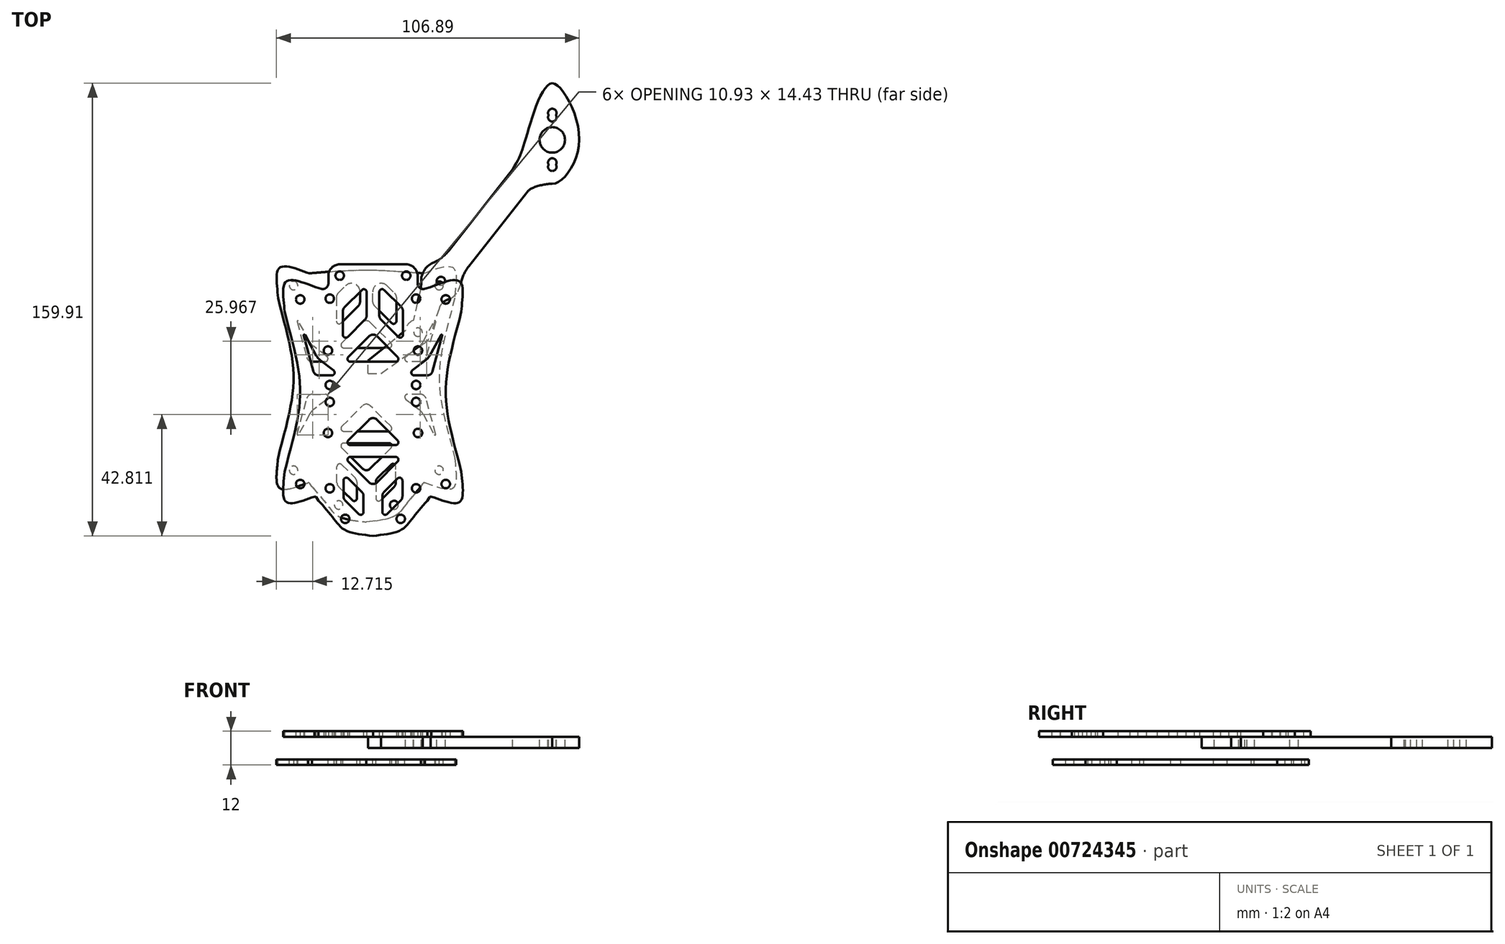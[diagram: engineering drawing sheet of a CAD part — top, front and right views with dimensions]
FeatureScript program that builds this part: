
annotation { "Feature Type Name" : "Feature", "Feature Type Description" : "" }
export const myFeature = defineFeature(function(context is Context, id is Id, definition is map)
    precondition{}
    {
        {
            var Q0;
            Q0=qCreatedBy(makeId("Top.planeOp"),FACE);
            var sketch = newSketch(context, id + "F0", { "sketchPlane" : qUnion([Q0])});
            skPoint(sketch, "E0.middle", {"position": v(0, -4.73) * mm});
            skLineSegment(sketch, "E1.bottom", {"start": v(25.7, 27.89) * mm, "end": v(-25.7, 27.89) * mm, "construction": true});
            skLineSegment(sketch, "E1.top", {"start": v(25.7, -37.35) * mm, "end": v(-25.7, -37.35) * mm, "construction": true});
            skLineSegment(sketch, "E1.left", {"start": v(25.7, 27.89) * mm, "end": v(25.7, -37.35) * mm, "construction": true});
            skLineSegment(sketch, "E1.right", {"start": v(-25.7, 27.89) * mm, "end": v(-25.7, -37.35) * mm, "construction": true});
            skLineSegment(sketch, "E2.bottom", {"start": v(-65, 77.77) * mm, "end": v(65, 77.77) * mm, "construction": true});
            skLineSegment(sketch, "E2.top", {"start": v(-65, -87.23) * mm, "end": v(65, -87.23) * mm, "construction": true});
            skLineSegment(sketch, "E2.left", {"start": v(-65, 77.77) * mm, "end": v(-65, -87.23) * mm, "construction": true});
            skLineSegment(sketch, "E2.right", {"start": v(65, 77.77) * mm, "end": v(65, -87.23) * mm, "construction": true});
            skCircle(sketch, "E3", {"center": v(65, 77.77) * mm, "radius": 4.5 * mm, "construction": true});
            skCircle(sketch, "E4", {"center": v(-65, 77.77) * mm, "radius": 4.5 * mm, "construction": true});
            skCircle(sketch, "E5", {"center": v(65, -87.23) * mm, "radius": 4.5 * mm, "construction": true});
            skCircle(sketch, "E6", {"center": v(-65, -87.23) * mm, "radius": 4.5 * mm, "construction": true});
            skCircle(sketch, "E7", {"center": v(65, 77.77) * mm, "radius": 8 * mm, "construction": true});
            skCircle(sketch, "E8", {"center": v(65, -87.23) * mm, "radius": 8 * mm, "construction": true});
            skCircle(sketch, "E9", {"center": v(-65, -87.23) * mm, "radius": 8 * mm, "construction": true});
            skCircle(sketch, "E10", {"center": v(-65, 77.77) * mm, "radius": 8 * mm, "construction": true});
            skCircle(sketch, "E11", {"center": v(65, 77.77) * mm, "radius": 9.5 * mm, "construction": true});
            skCircle(sketch, "E12", {"center": v(65, -87.23) * mm, "radius": 9.5 * mm, "construction": true});
            skCircle(sketch, "E13", {"center": v(-65, -87.23) * mm, "radius": 9.5 * mm, "construction": true});
            skCircle(sketch, "E14", {"center": v(-65, 77.77) * mm, "radius": 9.5 * mm, "construction": true});
            skCircle(sketch, "E15", {"center": v(65, 77.77) * mm, "radius": 14 * mm, "construction": true});
            skCircle(sketch, "E16", {"center": v(-65, 77.77) * mm, "radius": 14 * mm, "construction": true});
            skCircle(sketch, "E17", {"center": v(65, -87.23) * mm, "radius": 14 * mm, "construction": true});
            skCircle(sketch, "E18", {"center": v(-65, -87.23) * mm, "radius": 14 * mm, "construction": true});
            skCircle(sketch, "E19", {"center": v(65, 77.77) * mm, "radius": 63.5 * mm, "construction": true});
            skCircle(sketch, "E20", {"center": v(65, -87.23) * mm, "radius": 63.5 * mm, "construction": true});
            skCircle(sketch, "E21", {"center": v(-65, -87.23) * mm, "radius": 63.5 * mm, "construction": true});
            skCircle(sketch, "E22", {"center": v(-65, 77.77) * mm, "radius": 63.5 * mm, "construction": true});
            skLineSegment(sketch, "E23.bottom", {"start": v(-26.2, 21.46) * mm, "end": v(26.2, 21.46) * mm, "construction": true});
            skLineSegment(sketch, "E23.top", {"start": v(-26.19, -30.92) * mm, "end": v(26.2, -30.92) * mm, "construction": true});
            skLineSegment(sketch, "E23.left", {"start": v(-26.2, 21.46) * mm, "end": v(-26.2, -30.92) * mm, "construction": true});
            skLineSegment(sketch, "E23.right", {"start": v(26.2, 21.46) * mm, "end": v(26.2, -30.92) * mm, "construction": true});
            skCircle(sketch, "E24", {"center": v(25.7, 27.89) * mm, "radius": 1.5 * mm, "construction": true});
            skCircle(sketch, "E25", {"center": v(-25.7, 27.89) * mm, "radius": 1.5 * mm, "construction": true});
            skCircle(sketch, "E26", {"center": v(25.7, -37.35) * mm, "radius": 1.5 * mm, "construction": true});
            skCircle(sketch, "E27", {"center": v(-25.7, -37.35) * mm, "radius": 1.5 * mm, "construction": true});
            skLineSegment(sketch, "E28", {"start": v(-65, 77.77) * mm, "end": v(65, -87.23) * mm, "construction": true});
            skLineSegment(sketch, "E29", {"start": v(65, 77.77) * mm, "end": v(-65, -87.23) * mm, "construction": true});
            skLineSegment(sketch, "E30.bottom", {"start": v(-15.25, -8.35) * mm, "end": v(15.25, -8.35) * mm, "construction": true});
            skLineSegment(sketch, "E30.top", {"start": v(-15.25, -38.85) * mm, "end": v(15.25, -38.85) * mm, "construction": true});
            skLineSegment(sketch, "E30.left", {"start": v(-15.25, -8.35) * mm, "end": v(-15.25, -38.85) * mm, "construction": true});
            skLineSegment(sketch, "E30.right", {"start": v(15.25, -8.35) * mm, "end": v(15.25, -38.85) * mm, "construction": true});
            skPoint(sketch, "E30.middle", {"position": v(0, -23.6) * mm});
            skLineSegment(sketch, "E31.bottom", {"start": v(-15.25, 28.15) * mm, "end": v(15.25, 28.15) * mm, "construction": true});
            skLineSegment(sketch, "E31.top", {"start": v(-15.25, -2.35) * mm, "end": v(15.25, -2.35) * mm, "construction": true});
            skLineSegment(sketch, "E31.left", {"start": v(-15.25, 28.15) * mm, "end": v(-15.25, -2.35) * mm, "construction": true});
            skLineSegment(sketch, "E31.right", {"start": v(15.25, 28.15) * mm, "end": v(15.25, -2.35) * mm, "construction": true});
            skPoint(sketch, "E31.middle", {"position": v(0, 12.9) * mm});
            skLineSegment(sketch, "E32", {"start": v(0, -2.35) * mm, "end": v(0, -8.35) * mm, "construction": true});
            skLineSegment(sketch, "E33", {"start": v(0, 36.28) * mm, "end": v(-11.75, 36.28) * mm, "construction": true});
            skLineSegment(sketch, "E34", {"start": v(0, 36.28) * mm, "end": v(11.75, 36.28) * mm, "construction": true});
            skLineSegment(sketch, "E35", {"start": v(-25.7, 27.89) * mm, "end": v(-20.2, 32.22) * mm, "construction": true});
            skLineSegment(sketch, "E36", {"start": v(-25.7, 27.89) * mm, "end": v(-31.2, 23.56) * mm, "construction": true});
            skLineSegment(sketch, "E37", {"start": v(-25.7, 27.89) * mm, "end": v(-30.65, 34.17) * mm, "construction": true});
            skLineSegment(sketch, "E38", {"start": v(25.7, 27.89) * mm, "end": v(30.65, 34.17) * mm, "construction": true});
            skLineSegment(sketch, "E39", {"start": v(25.7, 27.89) * mm, "end": v(20.2, 32.22) * mm, "construction": true});
            skLineSegment(sketch, "E40", {"start": v(25.7, 27.89) * mm, "end": v(31.2, 23.56) * mm, "construction": true});
            skLineSegment(sketch, "E41", {"start": v(25.7, -37.35) * mm, "end": v(30.65, -43.64) * mm, "construction": true});
            skLineSegment(sketch, "E42", {"start": v(25.7, -37.35) * mm, "end": v(20.2, -41.68) * mm, "construction": true});
            skLineSegment(sketch, "E43", {"start": v(25.7, -37.35) * mm, "end": v(31.2, -33.02) * mm, "construction": true});
            skLineSegment(sketch, "E44", {"start": v(-25.7, -37.35) * mm, "end": v(-30.65, -43.64) * mm, "construction": true});
            skLineSegment(sketch, "E45", {"start": v(-25.7, -37.35) * mm, "end": v(-20.2, -41.68) * mm, "construction": true});
            skLineSegment(sketch, "E46", {"start": v(-25.7, -37.35) * mm, "end": v(-31.2, -33.02) * mm, "construction": true});
            skFitSpline(sketch, "E47", {"points": [v(-20.2, 32.22) * mm, v(-30.65, 34.17) * mm, v(-31.2, 23.56) * mm], "startDerivative": vector(-20.3, 7.46) * mm, "endDerivative": vector(0.93, -21.61) * mm});
            skFitSpline(sketch, "E48", {"points": [v(20.2, 32.22) * mm, v(30.65, 34.17) * mm, v(31.2, 23.56) * mm], "startDerivative": vector(20.3, 7.46) * mm, "endDerivative": vector(-0.93, -21.61) * mm});
            skLineSegment(sketch, "E49", {"start": v(-11.75, 36.28) * mm, "end": v(-15.75, 36.28) * mm, "construction": true});
            skLineSegment(sketch, "E50", {"start": v(11.75, 36.28) * mm, "end": v(15.75, 36.28) * mm, "construction": true});
            skCircle(sketch, "E51", {"center": v(-11.75, 36.28) * mm, "radius": 1.5 * mm});
            skCircle(sketch, "E52", {"center": v(11.75, 36.28) * mm, "radius": 1.5 * mm});
            skLineSegment(sketch, "E53", {"start": v(0, 36.28) * mm, "end": v(0, 40.28) * mm, "construction": true});
            skLineSegment(sketch, "E54", {"start": v(-15.75, 36.28) * mm, "end": v(-15.75, 36.28) * mm});
            skLineSegment(sketch, "E55", {"start": v(-11.75, 40.28) * mm, "end": v(0, 40.28) * mm});
            skLineSegment(sketch, "E56", {"start": v(0, 40.28) * mm, "end": v(11.75, 40.28) * mm});
            skLineSegment(sketch, "E57", {"start": v(15.75, 36.28) * mm, "end": v(15.75, 36.28) * mm});
            skPoint(sketch, "E58.visualSharp", {"position": v(-15.75, 40.28) * mm});
            skArc(sketch, "E58.filletArc", {"start": v(-11.75, 40.28) * mm, "mid": v(-14.58, 39.1) * mm, "end": v(-15.75, 36.28) * mm});
            skPoint(sketch, "E59.visualSharp", {"position": v(15.75, 40.28) * mm});
            skArc(sketch, "E59.filletArc", {"start": v(15.75, 36.28) * mm, "mid": v(14.58, 39.1) * mm, "end": v(11.75, 40.28) * mm});
            skLineSegment(sketch, "E60", {"start": v(-20.2, 32.22) * mm, "end": v(-18.34, 31.65) * mm});
            skLineSegment(sketch, "E61", {"start": v(-15.75, 33.56) * mm, "end": v(-15.75, 36.28) * mm});
            skPoint(sketch, "E62.visualSharp", {"position": v(-15.75, 30.85) * mm});
            skArc(sketch, "E62.filletArc", {"start": v(-18.34, 31.65) * mm, "mid": v(-16.56, 31.95) * mm, "end": v(-15.75, 33.56) * mm});
            skLineSegment(sketch, "E63", {"start": v(-15.75, 30.85) * mm, "end": v(0, 30.85) * mm, "construction": true});
            skLineSegment(sketch, "E64", {"start": v(0, 30.85) * mm, "end": v(15.75, 30.85) * mm, "construction": true});
            skLineSegment(sketch, "E65", {"start": v(20.2, 32.22) * mm, "end": v(18.34, 31.65) * mm});
            skLineSegment(sketch, "E66", {"start": v(15.75, 36.28) * mm, "end": v(15.75, 33.56) * mm});
            skPoint(sketch, "E67.visualSharp", {"position": v(15.75, 30.85) * mm});
            skArc(sketch, "E67.filletArc", {"start": v(15.75, 33.56) * mm, "mid": v(16.56, 31.95) * mm, "end": v(18.34, 31.65) * mm});
            skCircle(sketch, "E68", {"center": v(-15.25, -38.85) * mm, "radius": 1.5 * mm});
            skCircle(sketch, "E69", {"center": v(15.25, -38.85) * mm, "radius": 1.5 * mm});
            skLineSegment(sketch, "E70", {"start": v(0, -38.85) * mm, "end": v(0, -42.85) * mm, "construction": true});
            skLineSegment(sketch, "E71", {"start": v(-15.25, -38.85) * mm, "end": v(-19.25, -38.85) * mm, "construction": true});
            skLineSegment(sketch, "E72", {"start": v(15.25, -38.85) * mm, "end": v(19.25, -38.85) * mm, "construction": true});
            skLineSegment(sketch, "E73", {"start": v(-19.25, -43.2) * mm, "end": v(0, -43.2) * mm, "construction": true});
            skLineSegment(sketch, "E74", {"start": v(0, -43.2) * mm, "end": v(19.25, -43.2) * mm, "construction": true});
            skPoint(sketch, "E75.visualSharp", {"position": v(-19.25, -43.2) * mm});
            skPoint(sketch, "E76.visualSharp", {"position": v(19.25, -43.2) * mm});
            skCircle(sketch, "E77", {"center": v(-9.8, -49.64) * mm, "radius": 1.5 * mm});
            skCircle(sketch, "E78", {"center": v(9.8, -49.64) * mm, "radius": 1.5 * mm});
            skLineSegment(sketch, "E79", {"start": v(-9.8, -49.64) * mm, "end": v(0, -49.64) * mm, "construction": true});
            skLineSegment(sketch, "E80", {"start": v(0, -49.64) * mm, "end": v(9.8, -49.64) * mm, "construction": true});
            skFitSpline(sketch, "E81", {"points": [v(-31.2, 23.56) * mm, v(-25.7, -4.73) * mm, v(-31.2, -33.02) * mm], "startDerivative": vector(16.96, -67.18) * mm, "endDerivative": vector(-16.96, -67.18) * mm});
            skFitSpline(sketch, "E82", {"points": [v(31.2, 23.56) * mm, v(25.7, -4.73) * mm, v(31.2, -33.02) * mm], "startDerivative": vector(-16.96, -67.18) * mm, "endDerivative": vector(16.96, -67.18) * mm});
            skLineSegment(sketch, "E83", {"start": v(0, -49.64) * mm, "end": v(0, -55.64) * mm, "construction": true});
            skLineSegment(sketch, "E84", {"start": v(-9.8, -49.64) * mm, "end": v(-13.8, -49.64) * mm, "construction": true});
            skLineSegment(sketch, "E85", {"start": v(-9.8, -49.64) * mm, "end": v(-9.8, -53.64) * mm, "construction": true});
            skLineSegment(sketch, "E86", {"start": v(9.8, -49.64) * mm, "end": v(13.8, -49.64) * mm, "construction": true});
            skLineSegment(sketch, "E87", {"start": v(9.8, -49.64) * mm, "end": v(9.8, -53.64) * mm, "construction": true});
            skCircle(sketch, "E88", {"center": v(-25.7, 27.89) * mm, "radius": 1.5 * mm});
            skCircle(sketch, "E89", {"center": v(25.7, 27.89) * mm, "radius": 1.5 * mm});
            skCircle(sketch, "E90", {"center": v(-25.7, -37.35) * mm, "radius": 1.5 * mm});
            skCircle(sketch, "E91", {"center": v(25.7, -37.35) * mm, "radius": 1.5 * mm});
            skLineSegment(sketch, "E92", {"start": v(0, 27.89) * mm, "end": v(0, 36.28) * mm, "construction": true});
            skLineSegment(sketch, "E93", {"start": v(117.55, -29.37) * mm, "end": v(117.55, 4.6) * mm, "construction": true});
            skLineSegment(sketch, "E94", {"start": v(-19.04, -41.25) * mm, "end": v(0, -41.25) * mm, "construction": true});
            skLineSegment(sketch, "E95", {"start": v(0, -41.25) * mm, "end": v(19.04, -41.25) * mm, "construction": true});
            skFitSpline(sketch, "E96", {"points": [v(-19.25, -43.2) * mm, v(-13.8, -49.64) * mm, v(-9.8, -53.64) * mm, v(0, -55.64) * mm], "startDerivative": vector(17.01, -18.5) * mm, "endDerivative": vector(29.8, -3.11) * mm});
            skFitSpline(sketch, "E97", {"points": [v(19.25, -43.2) * mm, v(13.8, -49.64) * mm, v(9.8, -53.64) * mm, v(0, -55.64) * mm], "startDerivative": vector(-17.98, -19.6) * mm, "endDerivative": vector(-29.8, -3.11) * mm});
            skLineSegment(sketch, "E98", {"start": v(118.58, 5.6) * mm, "end": v(171.8, 3.95) * mm, "construction": true});
            skPoint(sketch, "E99.visualSharp", {"position": v(117.55, 5.63) * mm});
            skArc(sketch, "E99.filletArc", {"start": v(118.58, 5.6) * mm, "mid": v(117.85, 5.32) * mm, "end": v(117.55, 4.6) * mm, "construction": true});
            skPoint(sketch, "E100.visualSharp", {"position": v(19.04, -41.25) * mm});
            skPoint(sketch, "E101.visualSharp", {"position": v(-19.04, -41.25) * mm});
            skLineSegment(sketch, "E102.bottom", {"start": v(-13.78, 12.77) * mm, "end": v(13.78, 12.77) * mm, "construction": true});
            skLineSegment(sketch, "E102.top", {"start": v(-13.78, -22.23) * mm, "end": v(13.78, -22.23) * mm, "construction": true});
            skLineSegment(sketch, "E102.left", {"start": v(-13.78, 12.77) * mm, "end": v(-13.78, -22.23) * mm, "construction": true});
            skLineSegment(sketch, "E102.right", {"start": v(13.78, 12.77) * mm, "end": v(13.78, -22.23) * mm, "construction": true});
            skCircle(sketch, "E103", {"center": v(-15.25, -8.35) * mm, "radius": 1.5 * mm});
            skCircle(sketch, "E104", {"center": v(15.25, -8.35) * mm, "radius": 1.5 * mm});
            skCircle(sketch, "E105", {"center": v(15.25, -2.35) * mm, "radius": 1.5 * mm});
            skCircle(sketch, "E106", {"center": v(-15.25, -2.35) * mm, "radius": 1.5 * mm});
            skCircle(sketch, "E107", {"center": v(-15.25, 28.15) * mm, "radius": 1.5 * mm});
            skCircle(sketch, "E108", {"center": v(15.25, 28.15) * mm, "radius": 1.5 * mm});
            skLineSegment(sketch, "E109", {"start": v(0, 8.34) * mm, "end": v(-18.2, 8.34) * mm, "construction": true});
            skLineSegment(sketch, "E110", {"start": v(0, 8.34) * mm, "end": v(18.2, 8.34) * mm, "construction": true});
            skLineSegment(sketch, "E111", {"start": v(0, -4.73) * mm, "end": v(0, 9.53) * mm, "construction": true});
            skLineSegment(sketch, "E112", {"start": v(0, -4.73) * mm, "end": v(17, -4.73) * mm, "construction": true});
            skLineSegment(sketch, "E113.bottom", {"start": v(-15.9, 9.82) * mm, "end": v(15.9, 9.82) * mm, "construction": true});
            skLineSegment(sketch, "E113.top", {"start": v(-15.9, -19.29) * mm, "end": v(15.9, -19.29) * mm, "construction": true});
            skLineSegment(sketch, "E113.left", {"start": v(-15.9, 9.82) * mm, "end": v(-15.9, -19.29) * mm, "construction": true});
            skLineSegment(sketch, "E113.right", {"start": v(15.9, 9.82) * mm, "end": v(15.9, -19.29) * mm, "construction": true});
            skCircle(sketch, "E114", {"center": v(15.9, 9.82) * mm, "radius": 1.5 * mm});
            skCircle(sketch, "E115", {"center": v(15.9, -19.29) * mm, "radius": 1.5 * mm});
            skCircle(sketch, "E116", {"center": v(-15.9, -19.29) * mm, "radius": 1.5 * mm});
            skCircle(sketch, "E117", {"center": v(-15.9, 9.82) * mm, "radius": 1.5 * mm});
            skLineSegment(sketch, "E118", {"start": v(0, 21.19) * mm, "end": v(14.33, 21.19) * mm, "construction": true});
            skLineSegment(sketch, "E119", {"start": v(0, 21.19) * mm, "end": v(-14.33, 21.19) * mm, "construction": true});
            skPoint(sketch, "E120.middle", {"position": v(-14.33, 21.19) * mm});
            skPoint(sketch, "E121.middle", {"position": v(14.33, 21.19) * mm});
            skFitSpline(sketch, "E122", {"points": [v(-31.2, -33.02) * mm, v(-30.65, -43.64) * mm, v(-20.6, -41.83) * mm], "startDerivative": vector(-1.92, -24.87) * mm, "endDerivative": vector(23.17, 7.34) * mm});
            skLineSegment(sketch, "E123", {"start": v(-20.6, -41.83) * mm, "end": v(0, -41.83) * mm, "construction": true});
            skLineSegment(sketch, "E124", {"start": v(0, -41.83) * mm, "end": v(20.6, -41.83) * mm, "construction": true});
            skLineSegment(sketch, "E125", {"start": v(19.25, -43.2) * mm, "end": v(19.99, -42.02) * mm});
            skLineSegment(sketch, "E126", {"start": v(20.58, -41.82) * mm, "end": v(20.6, -41.83) * mm});
            skLineSegment(sketch, "E127", {"start": v(-19.25, -43.2) * mm, "end": v(-19.99, -42.02) * mm});
            skLineSegment(sketch, "E128", {"start": v(-20.58, -41.82) * mm, "end": v(-20.6, -41.83) * mm});
            skLineSegment(sketch, "E129", {"start": v(171.8, 3.95) * mm, "end": v(171.8, -18.5) * mm, "construction": true});
            skPoint(sketch, "E130.visualSharp", {"position": v(20.2, -41.68) * mm});
            skArc(sketch, "E130.filletArc", {"start": v(20.58, -41.82) * mm, "mid": v(20.25, -41.82) * mm, "end": v(19.99, -42.02) * mm});
            skPoint(sketch, "E131.visualSharp", {"position": v(-20.2, -41.68) * mm});
            skArc(sketch, "E131.filletArc", {"start": v(-19.99, -42.02) * mm, "mid": v(-20.25, -41.82) * mm, "end": v(-20.58, -41.82) * mm});
            skLineSegment(sketch, "E132", {"start": v(0, -4.73) * mm, "end": v(0, -1.43) * mm, "construction": true});
            skLineSegment(sketch, "E133.bottom", {"start": v(-5.5, 0.77) * mm, "end": v(5.5, 0.77) * mm, "construction": true});
            skLineSegment(sketch, "E133.top", {"start": v(-5.5, -10.23) * mm, "end": v(5.5, -10.23) * mm, "construction": true});
            skLineSegment(sketch, "E133.left", {"start": v(-5.5, 0.77) * mm, "end": v(-5.5, -10.23) * mm, "construction": true});
            skLineSegment(sketch, "E133.right", {"start": v(5.5, 0.77) * mm, "end": v(5.5, -10.23) * mm, "construction": true});
            skLineSegment(sketch, "E134.bottom", {"start": v(-7.98, 5.89) * mm, "end": v(7.98, 5.89) * mm});
            skPoint(sketch, "E134.middle", {"position": v(0, 7.86) * mm});
            skPoint(sketch, "E135.middle", {"position": v(0, -31.33) * mm});
            skPoint(sketch, "E136", {"position": v(0, -22.23) * mm});
            skPoint(sketch, "E137", {"position": v(0, -30.92) * mm});
            skLineSegment(sketch, "E138", {"start": v(-8.69, 7.6) * mm, "end": v(-1.41, 14.87) * mm});
            skLineSegment(sketch, "E139", {"start": v(1.41, 14.87) * mm, "end": v(8.69, 7.6) * mm});
            skPoint(sketch, "E140.visualSharp", {"position": v(0, 16.28) * mm});
            skArc(sketch, "E140.filletArc", {"start": v(1.41, 14.87) * mm, "mid": v(0, 15.46) * mm, "end": v(-1.41, 14.87) * mm});
            skPoint(sketch, "E141.visualSharp", {"position": v(-10.4, 5.89) * mm});
            skArc(sketch, "E141.filletArc", {"start": v(-8.69, 7.6) * mm, "mid": v(-8.9, 6.5) * mm, "end": v(-7.98, 5.89) * mm});
            skPoint(sketch, "E142.visualSharp", {"position": v(10.4, 5.89) * mm});
            skArc(sketch, "E142.filletArc", {"start": v(7.98, 5.89) * mm, "mid": v(8.9, 6.5) * mm, "end": v(8.69, 7.6) * mm});
            skPoint(sketch, "E143.visualSharp", {"position": v(0, -4.14) * mm});
            skLineSegment(sketch, "E144", {"start": v(1, 5.89) * mm, "end": v(1, 1.39) * mm, "construction": true});
            skPoint(sketch, "E145.middle", {"position": v(0, 4.86) * mm});
            skCircle(sketch, "E146", {"center": v(15.9, 9.82) * mm, "radius": 4.5 * mm, "construction": true});
            skCircle(sketch, "E147", {"center": v(-15.9, 9.82) * mm, "radius": 4.5 * mm, "construction": true});
            skCircle(sketch, "E148", {"center": v(15.9, -19.29) * mm, "radius": 4.5 * mm, "construction": true});
            skCircle(sketch, "E149", {"center": v(-15.9, -19.29) * mm, "radius": 4.5 * mm, "construction": true});
            skLineSegment(sketch, "E150", {"start": v(0, -4.73) * mm, "end": v(-15.9, 9.82) * mm, "construction": true});
            skLineSegment(sketch, "E151", {"start": v(0, -4.73) * mm, "end": v(15.9, 9.82) * mm, "construction": true});
            skLineSegment(sketch, "E152", {"start": v(15.9, 9.82) * mm, "end": v(25.7, 27.89) * mm, "construction": true});
            skLineSegment(sketch, "E153", {"start": v(-15.9, 9.82) * mm, "end": v(-25.7, 27.89) * mm, "construction": true});
            skLineSegment(sketch, "E154", {"start": v(0, -4.73) * mm, "end": v(-15.9, -19.29) * mm, "construction": true});
            skLineSegment(sketch, "E155", {"start": v(-15.9, -19.29) * mm, "end": v(-25.7, -37.35) * mm, "construction": true});
            skLineSegment(sketch, "E156", {"start": v(0, -4.73) * mm, "end": v(15.9, -19.29) * mm, "construction": true});
            skLineSegment(sketch, "E157", {"start": v(15.9, -19.29) * mm, "end": v(25.7, -37.35) * mm, "construction": true});
            skLineSegment(sketch, "E158", {"start": v(-2.25, 22.16) * mm, "end": v(-2.25, 30.51) * mm});
            skLineSegment(sketch, "E159", {"start": v(2.25, 22.16) * mm, "end": v(2.25, 30.51) * mm});
            skLineSegment(sketch, "E160", {"start": v(-3.95, 31.22) * mm, "end": v(-10.02, 25.16) * mm});
            skLineSegment(sketch, "E161", {"start": v(-10.6, 23.74) * mm, "end": v(-10.6, 15.38) * mm});
            skLineSegment(sketch, "E162", {"start": v(3.95, 31.22) * mm, "end": v(10.02, 25.16) * mm});
            skLineSegment(sketch, "E163", {"start": v(10.6, 23.74) * mm, "end": v(10.6, 15.38) * mm});
            skLineSegment(sketch, "E164", {"start": v(-8.9, 14.68) * mm, "end": v(-2.83, 20.74) * mm});
            skLineSegment(sketch, "E165", {"start": v(2.83, 20.74) * mm, "end": v(8.9, 14.68) * mm});
            skPoint(sketch, "E166.visualSharp", {"position": v(-2.25, 32.93) * mm});
            skArc(sketch, "E166.filletArc", {"start": v(-2.25, 30.51) * mm, "mid": v(-2.86, 31.44) * mm, "end": v(-3.95, 31.22) * mm});
            skPoint(sketch, "E167.visualSharp", {"position": v(-10.6, 24.57) * mm});
            skArc(sketch, "E167.filletArc", {"start": v(-10.02, 25.16) * mm, "mid": v(-10.45, 24.5) * mm, "end": v(-10.6, 23.74) * mm});
            skPoint(sketch, "E168.visualSharp", {"position": v(-2.25, 21.33) * mm});
            skArc(sketch, "E168.filletArc", {"start": v(-2.83, 20.74) * mm, "mid": v(-2.4, 21.4) * mm, "end": v(-2.25, 22.16) * mm});
            skPoint(sketch, "E169.visualSharp", {"position": v(2.25, 21.33) * mm});
            skArc(sketch, "E169.filletArc", {"start": v(2.25, 22.16) * mm, "mid": v(2.4, 21.4) * mm, "end": v(2.83, 20.74) * mm});
            skPoint(sketch, "E170.visualSharp", {"position": v(10.6, 24.57) * mm});
            skArc(sketch, "E170.filletArc", {"start": v(10.6, 23.74) * mm, "mid": v(10.45, 24.5) * mm, "end": v(10.02, 25.16) * mm});
            skPoint(sketch, "E171.visualSharp", {"position": v(2.25, 32.93) * mm});
            skArc(sketch, "E171.filletArc", {"start": v(3.95, 31.22) * mm, "mid": v(2.86, 31.44) * mm, "end": v(2.25, 30.51) * mm});
            skPoint(sketch, "E172.visualSharp", {"position": v(10.6, 12.97) * mm});
            skArc(sketch, "E172.filletArc", {"start": v(8.9, 14.68) * mm, "mid": v(9.99, 14.46) * mm, "end": v(10.6, 15.38) * mm});
            skPoint(sketch, "E173.visualSharp", {"position": v(-10.6, 12.97) * mm});
            skArc(sketch, "E173.filletArc", {"start": v(-10.6, 15.38) * mm, "mid": v(-9.99, 14.46) * mm, "end": v(-8.9, 14.68) * mm});
            skLineSegment(sketch, "E174", {"start": v(0, -27.75) * mm, "end": v(-7.99, -27.75) * mm});
            skLineSegment(sketch, "E175", {"start": v(0, -27.75) * mm, "end": v(7.99, -27.75) * mm});
            skLineSegment(sketch, "E176", {"start": v(-8.7, -29.46) * mm, "end": v(-1.41, -36.74) * mm});
            skLineSegment(sketch, "E177", {"start": v(8.7, -29.46) * mm, "end": v(1.41, -36.74) * mm});
            skPoint(sketch, "E178.visualSharp", {"position": v(10.4, -27.75) * mm});
            skArc(sketch, "E178.filletArc", {"start": v(8.7, -29.46) * mm, "mid": v(8.9, -28.37) * mm, "end": v(7.99, -27.75) * mm});
            skPoint(sketch, "E179.visualSharp", {"position": v(-10.4, -27.75) * mm});
            skArc(sketch, "E179.filletArc", {"start": v(-7.99, -27.75) * mm, "mid": v(-8.9, -28.37) * mm, "end": v(-8.7, -29.46) * mm});
            skPoint(sketch, "E180.visualSharp", {"position": v(0, -38.15) * mm});
            skArc(sketch, "E180.filletArc", {"start": v(-1.41, -36.74) * mm, "mid": v(0, -37.32) * mm, "end": v(1.41, -36.74) * mm});
            skFitSpline(sketch, "E181", {"points": [v(31.2, -33.02) * mm, v(30.65, -43.64) * mm, v(20.6, -41.83) * mm], "startDerivative": vector(1.93, -24.89) * mm, "endDerivative": vector(-23.2, 7.39) * mm});
            skLineSegment(sketch, "E182", {"start": v(-8.7, -35.4) * mm, "end": v(-3.91, -40.17) * mm});
            skLineSegment(sketch, "E183", {"start": v(8.7, -35.4) * mm, "end": v(3.91, -40.17) * mm});
            skLineSegment(sketch, "E184", {"start": v(-3.33, -41.59) * mm, "end": v(-3.33, -47.23) * mm});
            skLineSegment(sketch, "E185", {"start": v(-5.04, -47.93) * mm, "end": v(-9.81, -43.15) * mm});
            skLineSegment(sketch, "E186", {"start": v(-10.4, -41.74) * mm, "end": v(-10.4, -36.1) * mm});
            skLineSegment(sketch, "E187", {"start": v(3.33, -41.59) * mm, "end": v(3.33, -47.23) * mm});
            skLineSegment(sketch, "E188", {"start": v(5.04, -47.93) * mm, "end": v(9.81, -43.15) * mm});
            skLineSegment(sketch, "E189", {"start": v(10.4, -41.74) * mm, "end": v(10.4, -36.1) * mm});
            skPoint(sketch, "E190.visualSharp", {"position": v(10.4, -33.69) * mm});
            skArc(sketch, "E190.filletArc", {"start": v(10.4, -36.1) * mm, "mid": v(9.78, -35.18) * mm, "end": v(8.7, -35.4) * mm});
            skPoint(sketch, "E191.visualSharp", {"position": v(3.33, -49.64) * mm});
            skArc(sketch, "E191.filletArc", {"start": v(3.33, -47.23) * mm, "mid": v(3.95, -48.15) * mm, "end": v(5.04, -47.93) * mm});
            skPoint(sketch, "E192.visualSharp", {"position": v(-3.33, -49.64) * mm});
            skArc(sketch, "E192.filletArc", {"start": v(-5.04, -47.93) * mm, "mid": v(-3.95, -48.15) * mm, "end": v(-3.33, -47.23) * mm});
            skPoint(sketch, "E193.visualSharp", {"position": v(-10.4, -33.69) * mm});
            skArc(sketch, "E193.filletArc", {"start": v(-8.7, -35.4) * mm, "mid": v(-9.78, -35.18) * mm, "end": v(-10.4, -36.1) * mm});
            skPoint(sketch, "E194.visualSharp", {"position": v(-3.33, -40.76) * mm});
            skArc(sketch, "E194.filletArc", {"start": v(-3.33, -41.59) * mm, "mid": v(-3.48, -40.82) * mm, "end": v(-3.91, -40.17) * mm});
            skPoint(sketch, "E195.visualSharp", {"position": v(-10.4, -42.57) * mm});
            skArc(sketch, "E195.filletArc", {"start": v(-10.4, -41.74) * mm, "mid": v(-10.25, -42.5) * mm, "end": v(-9.81, -43.15) * mm});
            skPoint(sketch, "E196.visualSharp", {"position": v(3.33, -40.76) * mm});
            skArc(sketch, "E196.filletArc", {"start": v(3.91, -40.17) * mm, "mid": v(3.48, -40.82) * mm, "end": v(3.33, -41.59) * mm});
            skPoint(sketch, "E197.visualSharp", {"position": v(10.4, -42.57) * mm});
            skArc(sketch, "E197.filletArc", {"start": v(9.81, -43.15) * mm, "mid": v(10.25, -42.5) * mm, "end": v(10.4, -41.74) * mm});
            skLineSegment(sketch, "E198", {"start": v(0, -23.6) * mm, "end": v(-7.99, -23.6) * mm});
            skLineSegment(sketch, "E199", {"start": v(0, -23.6) * mm, "end": v(7.99, -23.6) * mm});
            skLineSegment(sketch, "E200", {"start": v(-8.7, -21.89) * mm, "end": v(-1.41, -14.61) * mm});
            skLineSegment(sketch, "E201", {"start": v(8.7, -21.89) * mm, "end": v(1.41, -14.61) * mm});
            skPoint(sketch, "E202.visualSharp", {"position": v(0, -13.2) * mm});
            skArc(sketch, "E202.filletArc", {"start": v(1.41, -14.61) * mm, "mid": v(0, -14.02) * mm, "end": v(-1.41, -14.61) * mm});
            skPoint(sketch, "E203.visualSharp", {"position": v(-10.4, -23.6) * mm});
            skArc(sketch, "E203.filletArc", {"start": v(-8.7, -21.89) * mm, "mid": v(-8.9, -22.98) * mm, "end": v(-7.99, -23.6) * mm});
            skPoint(sketch, "E204.visualSharp", {"position": v(10.4, -23.6) * mm});
            skArc(sketch, "E204.filletArc", {"start": v(7.99, -23.6) * mm, "mid": v(8.9, -22.98) * mm, "end": v(8.7, -21.89) * mm});
            skLineSegment(sketch, "E205", {"start": v(17, -4.73) * mm, "end": v(20, -4.73) * mm, "construction": true});
            skCircle(sketch, "E206", {"center": v(25.7, 27.89) * mm, "radius": 7 * mm, "construction": true});
            skLineSegment(sketch, "E207", {"start": v(19.97, 8) * mm, "end": v(24.01, 15.34) * mm});
            skLineSegment(sketch, "E208", {"start": v(24.47, 15.15) * mm, "end": v(21.06, 2.52) * mm});
            skLineSegment(sketch, "E209", {"start": v(19.13, 1.04) * mm, "end": v(14.55, 1.04) * mm});
            skLineSegment(sketch, "E210", {"start": v(13.94, 2.83) * mm, "end": v(18.64, 6.44) * mm});
            skPoint(sketch, "E211.visualSharp", {"position": v(25.02, 17.15) * mm});
            skArc(sketch, "E211.filletArc", {"start": v(24.47, 15.15) * mm, "mid": v(24.33, 15.45) * mm, "end": v(24.01, 15.34) * mm});
            skPoint(sketch, "E212.visualSharp", {"position": v(20.66, 1.04) * mm});
            skArc(sketch, "E212.filletArc", {"start": v(19.13, 1.04) * mm, "mid": v(20.34, 1.45) * mm, "end": v(21.06, 2.52) * mm});
            skPoint(sketch, "E213.visualSharp", {"position": v(11.62, 1.04) * mm});
            skArc(sketch, "E213.filletArc", {"start": v(13.94, 2.83) * mm, "mid": v(13.6, 1.72) * mm, "end": v(14.55, 1.04) * mm});
            skPoint(sketch, "E214.visualSharp", {"position": v(19.46, 7.08) * mm});
            skArc(sketch, "E214.filletArc", {"start": v(18.64, 6.44) * mm, "mid": v(19.38, 7.15) * mm, "end": v(19.97, 8) * mm});
            skLineSegment(sketch, "E215", {"start": v(11.62, 1.04) * mm, "end": v(0, 1.04) * mm, "construction": true});
            skPoint(sketch, "E215.endSnap0", {"position": v(0, 0.77) * mm});
            skLineSegment(sketch, "E216", {"start": v(0, 1.04) * mm, "end": v(-11.62, 1.04) * mm, "construction": true});
            skLineSegment(sketch, "E217", {"start": v(-14.55, 1.04) * mm, "end": v(-19.13, 1.04) * mm});
            skLineSegment(sketch, "E218", {"start": v(19.46, 7.08) * mm, "end": v(0, 7.08) * mm, "construction": true});
            skLineSegment(sketch, "E219", {"start": v(0, 7.08) * mm, "end": v(-19.46, 7.08) * mm, "construction": true});
            skLineSegment(sketch, "E220", {"start": v(25.02, 17.15) * mm, "end": v(0, 17.15) * mm, "construction": true});
            skLineSegment(sketch, "E221", {"start": v(0, 17.15) * mm, "end": v(-25.02, 17.15) * mm, "construction": true});
            skLineSegment(sketch, "E222", {"start": v(-24.47, 15.15) * mm, "end": v(-21.06, 2.52) * mm});
            skLineSegment(sketch, "E223", {"start": v(-13.94, 2.83) * mm, "end": v(-18.64, 6.44) * mm});
            skLineSegment(sketch, "E224", {"start": v(-19.97, 8) * mm, "end": v(-24.01, 15.34) * mm});
            skPoint(sketch, "E225.visualSharp", {"position": v(-25.02, 17.15) * mm});
            skArc(sketch, "E225.filletArc", {"start": v(-24.01, 15.34) * mm, "mid": v(-24.33, 15.45) * mm, "end": v(-24.47, 15.15) * mm});
            skPoint(sketch, "E226.visualSharp", {"position": v(-11.62, 1.04) * mm});
            skArc(sketch, "E226.filletArc", {"start": v(-14.55, 1.04) * mm, "mid": v(-13.6, 1.72) * mm, "end": v(-13.94, 2.83) * mm});
            skPoint(sketch, "E227.visualSharp", {"position": v(-20.66, 1.04) * mm});
            skArc(sketch, "E227.filletArc", {"start": v(-21.06, 2.52) * mm, "mid": v(-20.34, 1.45) * mm, "end": v(-19.13, 1.04) * mm});
            skPoint(sketch, "E228.visualSharp", {"position": v(-19.46, 7.08) * mm});
            skArc(sketch, "E228.filletArc", {"start": v(-19.97, 8) * mm, "mid": v(-19.38, 7.15) * mm, "end": v(-18.64, 6.44) * mm});
            skSolve(sketch);
        }
        {
            var Q0;
            Q0=makeQuery(id+"F0.imprint","IMPRINT",FACE,{"disambiguationData":[TD([[makeQuery(id+"F0.imprint","IMPRINT",EDGE,{"derivedFrom":sQuery(id+"F0.wireOp",EDGE,"E47")}),1.0]])]});
            extrude(context, id + "F1", {"entities" : qUnion([Q0]), "depth" : 2 * mm});
        }
        {
            var Q0;
            Q0=qCreatedBy(makeId("Top.planeOp"),FACE);
            var sketch = newSketch(context, id + "F2", { "sketchPlane" : qUnion([Q0])});
            skPoint(sketch, "E229.middle", {"position": v(-1.68, 1.77) * mm});
            skLineSegment(sketch, "E230.bottom", {"start": v(24.01, 34.4) * mm, "end": v(-27.36, 34.4) * mm, "construction": true});
            skLineSegment(sketch, "E230.top", {"start": v(24.01, -30.86) * mm, "end": v(-27.36, -30.86) * mm, "construction": true});
            skLineSegment(sketch, "E230.left", {"start": v(24.01, 34.4) * mm, "end": v(24.01, -30.86) * mm, "construction": true});
            skLineSegment(sketch, "E230.right", {"start": v(-27.36, 34.4) * mm, "end": v(-27.36, -30.86) * mm, "construction": true});
            skLineSegment(sketch, "E231.bottom", {"start": v(-66.68, 84.27) * mm, "end": v(63.32, 84.27) * mm, "construction": true});
            skLineSegment(sketch, "E231.top", {"start": v(-66.68, -80.73) * mm, "end": v(63.32, -80.73) * mm, "construction": true});
            skLineSegment(sketch, "E231.left", {"start": v(-66.68, 84.27) * mm, "end": v(-66.68, -80.73) * mm, "construction": true});
            skLineSegment(sketch, "E231.right", {"start": v(63.32, 84.27) * mm, "end": v(63.32, -80.73) * mm, "construction": true});
            skCircle(sketch, "E232", {"center": v(63.32, 84.27) * mm, "radius": 4.5 * mm, "construction": true});
            skCircle(sketch, "E233", {"center": v(-66.68, 84.27) * mm, "radius": 4.5 * mm, "construction": true});
            skCircle(sketch, "E234", {"center": v(63.32, -80.73) * mm, "radius": 4.5 * mm, "construction": true});
            skCircle(sketch, "E235", {"center": v(-66.68, -80.73) * mm, "radius": 4.5 * mm, "construction": true});
            skCircle(sketch, "E236", {"center": v(63.32, 84.27) * mm, "radius": 8 * mm, "construction": true});
            skCircle(sketch, "E237", {"center": v(63.32, -80.73) * mm, "radius": 8 * mm, "construction": true});
            skCircle(sketch, "E238", {"center": v(-66.68, -80.73) * mm, "radius": 8 * mm, "construction": true});
            skCircle(sketch, "E239", {"center": v(-66.68, 84.27) * mm, "radius": 8 * mm, "construction": true});
            skCircle(sketch, "E240", {"center": v(63.32, 84.27) * mm, "radius": 9.5 * mm, "construction": true});
            skCircle(sketch, "E241", {"center": v(63.32, -80.73) * mm, "radius": 9.5 * mm, "construction": true});
            skCircle(sketch, "E242", {"center": v(-66.68, -80.73) * mm, "radius": 9.5 * mm, "construction": true});
            skCircle(sketch, "E243", {"center": v(-66.68, 84.27) * mm, "radius": 9.5 * mm, "construction": true});
            skCircle(sketch, "E244", {"center": v(63.32, 84.27) * mm, "radius": 14 * mm, "construction": true});
            skCircle(sketch, "E245", {"center": v(-66.68, 84.27) * mm, "radius": 14 * mm, "construction": true});
            skCircle(sketch, "E246", {"center": v(63.32, -80.73) * mm, "radius": 14 * mm, "construction": true});
            skCircle(sketch, "E247", {"center": v(-66.68, -80.73) * mm, "radius": 14 * mm, "construction": true});
            skCircle(sketch, "E248", {"center": v(63.32, 84.27) * mm, "radius": 63.5 * mm, "construction": true});
            skCircle(sketch, "E249", {"center": v(63.32, -80.73) * mm, "radius": 63.5 * mm, "construction": true});
            skCircle(sketch, "E250", {"center": v(-66.68, -80.73) * mm, "radius": 63.5 * mm, "construction": true});
            skCircle(sketch, "E251", {"center": v(-66.68, 84.27) * mm, "radius": 63.5 * mm, "construction": true});
            skLineSegment(sketch, "E252.bottom", {"start": v(-27.87, 27.96) * mm, "end": v(24.51, 27.96) * mm, "construction": true});
            skLineSegment(sketch, "E252.top", {"start": v(-27.87, -24.42) * mm, "end": v(24.51, -24.42) * mm, "construction": true});
            skLineSegment(sketch, "E252.left", {"start": v(-27.87, 27.96) * mm, "end": v(-27.87, -24.42) * mm, "construction": true});
            skLineSegment(sketch, "E252.right", {"start": v(24.51, 27.96) * mm, "end": v(24.51, -24.42) * mm, "construction": true});
            skCircle(sketch, "E253", {"center": v(24.01, 34.4) * mm, "radius": 3.57 * mm, "construction": true});
            skCircle(sketch, "E254", {"center": v(-27.36, 34.4) * mm, "radius": 3.57 * mm, "construction": true});
            skCircle(sketch, "E255", {"center": v(24.01, -30.86) * mm, "radius": 3.57 * mm, "construction": true});
            skCircle(sketch, "E256", {"center": v(-27.36, -30.86) * mm, "radius": 3.57 * mm, "construction": true});
            skLineSegment(sketch, "E257", {"start": v(-66.68, 84.27) * mm, "end": v(63.32, -80.73) * mm, "construction": true});
            skLineSegment(sketch, "E258", {"start": v(63.32, 84.27) * mm, "end": v(-66.68, -80.73) * mm, "construction": true});
            skLineSegment(sketch, "E259.bottom", {"start": v(-15.25, -12) * mm, "end": v(15.25, -12) * mm, "construction": true});
            skLineSegment(sketch, "E259.top", {"start": v(-15.25, -42.5) * mm, "end": v(15.25, -42.5) * mm, "construction": true});
            skLineSegment(sketch, "E259.left", {"start": v(-15.25, -12) * mm, "end": v(-15.25, -42.5) * mm, "construction": true});
            skLineSegment(sketch, "E259.right", {"start": v(15.25, -12) * mm, "end": v(15.25, -42.5) * mm, "construction": true});
            skPoint(sketch, "E259.middle", {"position": v(0, -27.25) * mm});
            skLineSegment(sketch, "E260.bottom", {"start": v(-16.93, 29) * mm, "end": v(13.57, 29) * mm, "construction": true});
            skLineSegment(sketch, "E260.top", {"start": v(-16.93, -1.5) * mm, "end": v(13.57, -1.5) * mm, "construction": true});
            skLineSegment(sketch, "E260.left", {"start": v(-16.93, 29) * mm, "end": v(-16.93, -1.5) * mm, "construction": true});
            skPoint(sketch, "E260.middle", {"position": v(-1.68, 13.75) * mm});
            skLineSegment(sketch, "E261", {"start": v(-1.68, -1.5) * mm, "end": v(-1.68, -12) * mm, "construction": true});
            skCircle(sketch, "E262", {"center": v(24.01, 34.4) * mm, "radius": 1.5 * mm, "construction": true});
            skCircle(sketch, "E263", {"center": v(-27.36, 34.4) * mm, "radius": 1.5 * mm, "construction": true});
            skCircle(sketch, "E264", {"center": v(24.01, -30.86) * mm, "radius": 1.5 * mm, "construction": true});
            skCircle(sketch, "E265", {"center": v(-27.36, -30.86) * mm, "radius": 1.5 * mm, "construction": true});
            skCircle(sketch, "E266", {"center": v(24.01, 34.4) * mm, "radius": 7 * mm, "construction": true});
            skLineSegment(sketch, "E267.bottom", {"start": v(-19.18, 19.27) * mm, "end": v(15.82, 19.27) * mm, "construction": true});
            skLineSegment(sketch, "E267.top", {"start": v(-19.18, -15.73) * mm, "end": v(15.82, -15.73) * mm, "construction": true});
            skLineSegment(sketch, "E267.left", {"start": v(-19.18, 19.27) * mm, "end": v(-19.18, -15.73) * mm, "construction": true});
            skLineSegment(sketch, "E268", {"start": v(63.32, 84.27) * mm, "end": v(77.32, 84.27) * mm, "construction": true});
            skLineSegment(sketch, "E269", {"start": v(63.32, 84.27) * mm, "end": v(63.32, 98.27) * mm, "construction": true});
            skCircle(sketch, "E270", {"center": v(63.32, 93.77) * mm, "radius": 1.5 * mm, "construction": true});
            skCircle(sketch, "E271", {"center": v(63.32, 92.27) * mm, "radius": 1.5 * mm, "construction": true});
            skCircle(sketch, "E272", {"center": v(63.32, 76.27) * mm, "radius": 1.5 * mm, "construction": true});
            skCircle(sketch, "E273", {"center": v(63.32, 74.77) * mm, "radius": 1.5 * mm, "construction": true});
            skCircle(sketch, "E274", {"center": v(63.32, 84.27) * mm, "radius": 15.5 * mm, "construction": true});
            skCircle(sketch, "E275", {"center": v(63.32, 84.27) * mm, "radius": 20 * mm, "construction": true});
            skCircle(sketch, "E276", {"center": v(63.32, 84.27) * mm, "radius": 23.5 * mm, "construction": true});
            skLineSegment(sketch, "E277", {"start": v(63.32, 98.27) * mm, "end": v(63.32, 107.77) * mm, "construction": true});
            skLineSegment(sketch, "E278", {"start": v(77.32, 84.27) * mm, "end": v(86.82, 84.27) * mm, "construction": true});
            skLineSegment(sketch, "E279", {"start": v(59.32, 103.86) * mm, "end": v(63.32, 103.86) * mm, "construction": true});
            skCircle(sketch, "E280", {"center": v(24.01, 34.4) * mm, "radius": 1.5 * mm});
            skLineSegment(sketch, "E281", {"start": v(54.66, 73.27) * mm, "end": v(51.13, 76.06) * mm, "construction": true});
            skLineSegment(sketch, "E282", {"start": v(54.66, 73.27) * mm, "end": v(58.2, 70.49) * mm, "construction": true});
            skLineSegment(sketch, "E283", {"start": v(51.13, 76.06) * mm, "end": v(23.82, 41.4) * mm, "construction": true});
            skLineSegment(sketch, "E284", {"start": v(58.2, 70.49) * mm, "end": v(30.87, 35.8) * mm, "construction": true});
            skLineSegment(sketch, "E285", {"start": v(23.82, 41.4) * mm, "end": v(17.16, 32.95) * mm, "construction": true});
            skLineSegment(sketch, "E286", {"start": v(30.87, 35.8) * mm, "end": v(24.25, 27.4) * mm, "construction": true});
            skLineSegment(sketch, "E287", {"start": v(63.32, 84.27) * mm, "end": v(55.86, 90.15) * mm, "construction": true});
            skLineSegment(sketch, "E288", {"start": v(63.32, 84.27) * mm, "end": v(70.79, 78.39) * mm, "construction": true});
            skLineSegment(sketch, "E289", {"start": v(49.36, 73.81) * mm, "end": v(56.43, 68.24) * mm, "construction": true});
            skLineSegment(sketch, "E290", {"start": v(63.32, 84.27) * mm, "end": v(69.2, 91.73) * mm, "construction": true});
            skLineSegment(sketch, "E291", {"start": v(26.82, 45.2) * mm, "end": v(49.36, 73.81) * mm});
            skArc(sketch, "E292", {"start": v(21.15, 40.8) * mm, "mid": v(18.04, 38.06) * mm, "end": v(17.02, 34.05) * mm});
            skArc(sketch, "E293", {"start": v(26.4, 27.82) * mm, "mid": v(29.34, 29.86) * mm, "end": v(30.89, 33.1) * mm});
            skLineSegment(sketch, "E294", {"start": v(-1.68, 1.77) * mm, "end": v(-1.68, 19.27) * mm, "construction": true});
            skLineSegment(sketch, "E295", {"start": v(-1.68, 1.77) * mm, "end": v(11.81, 1.77) * mm, "construction": true});
            skPoint(sketch, "E296", {"position": v(68.28, 90.55) * mm});
            skLineSegment(sketch, "E297", {"start": v(55.86, 90.15) * mm, "end": v(44.87, 98.81) * mm, "construction": true});
            skLineSegment(sketch, "E298", {"start": v(70.79, 78.39) * mm, "end": v(81.78, 69.73) * mm, "construction": true});
            skLineSegment(sketch, "E299", {"start": v(69.2, 91.73) * mm, "end": v(77.87, 102.73) * mm, "construction": true});
            skCircle(sketch, "E300", {"center": v(63.32, 84.27) * mm, "radius": 4.5 * mm});
            skArc(sketch, "E301", {"start": v(64.62, 93.02) * mm, "mid": v(63.32, 95.27) * mm, "end": v(62.03, 93.02) * mm});
            skArc(sketch, "E302", {"start": v(62.03, 93.02) * mm, "mid": v(63.32, 90.77) * mm, "end": v(64.62, 93.02) * mm});
            skArc(sketch, "E303", {"start": v(64.62, 75.52) * mm, "mid": v(63.32, 77.77) * mm, "end": v(62.03, 75.52) * mm});
            skArc(sketch, "E304", {"start": v(62.03, 75.52) * mm, "mid": v(63.32, 73.27) * mm, "end": v(64.62, 75.52) * mm});
            skLineSegment(sketch, "E305", {"start": v(63.32, 84.27) * mm, "end": v(72.1, 93.05) * mm, "construction": true});
            skPoint(sketch, "E306", {"position": v(68.98, 89.93) * mm});
            skLineSegment(sketch, "E307", {"start": v(63.32, 103.86) * mm, "end": v(67.32, 103.86) * mm, "construction": true});
            skLineSegment(sketch, "E308", {"start": v(63.32, 98.27) * mm, "end": v(60.62, 98.27) * mm, "construction": true});
            skLineSegment(sketch, "E309", {"start": v(63.32, 98.27) * mm, "end": v(66.02, 98.27) * mm, "construction": true});
            skLineSegment(sketch, "E310", {"start": v(58.53, 97.51) * mm, "end": v(63.32, 97.51) * mm, "construction": true});
            skLineSegment(sketch, "E311", {"start": v(63.32, 97.51) * mm, "end": v(68.12, 97.51) * mm, "construction": true});
            skLineSegment(sketch, "E312", {"start": v(12.11, 19.27) * mm, "end": v(-1.68, 19.27) * mm, "construction": true});
            skCircle(sketch, "E313", {"center": v(15.9, 16.32) * mm, "radius": 1.5 * mm});
            skCircle(sketch, "E314", {"center": v(15.9, 16.32) * mm, "radius": 4.5 * mm, "construction": true});
            skLineSegment(sketch, "E315", {"start": v(16.77, 31.26) * mm, "end": v(14.24, 20.5) * mm});
            skLineSegment(sketch, "E316", {"start": v(14.24, 20.5) * mm, "end": v(11.44, 16.96) * mm, "construction": true});
            skLineSegment(sketch, "E317", {"start": v(14.24, 20.5) * mm, "end": v(20.35, 15.68) * mm, "construction": true});
            skLineSegment(sketch, "E318", {"start": v(11.44, 16.96) * mm, "end": v(17.56, 12.14) * mm, "construction": true});
            skLineSegment(sketch, "E319", {"start": v(17.56, 12.14) * mm, "end": v(20.35, 15.68) * mm, "construction": true});
            skLineSegment(sketch, "E320", {"start": v(23.35, 24.7) * mm, "end": v(20.35, 15.68) * mm});
            skLineSegment(sketch, "E321", {"start": v(-1.68, 1.77) * mm, "end": v(-1.68, 6.27) * mm});
            skLineSegment(sketch, "E322", {"start": v(-1.68, 1.77) * mm, "end": v(2.82, 1.77) * mm});
            skLineSegment(sketch, "E323", {"start": v(-1.68, 6.27) * mm, "end": v(11.44, 16.96) * mm});
            skLineSegment(sketch, "E324", {"start": v(2.82, 1.77) * mm, "end": v(17.56, 12.14) * mm});
            skArc(sketch, "E325", {"start": v(17.56, 12.14) * mm, "mid": v(19.43, 13.54) * mm, "end": v(20.35, 15.68) * mm});
            skArc(sketch, "E326", {"start": v(14.24, 20.5) * mm, "mid": v(12.36, 19.1) * mm, "end": v(11.44, 16.96) * mm});
            skLineSegment(sketch, "E327", {"start": v(15.9, 16.32) * mm, "end": v(0, 16.32) * mm, "construction": true});
            skLineSegment(sketch, "E328", {"start": v(15.9, 16.32) * mm, "end": v(15.9, 1.77) * mm, "construction": true});
            skFitSpline(sketch, "E329", {"points": [v(49.36, 73.81) * mm, v(53.82, 84.27) * mm, v(63.32, 104.27) * mm], "startDerivative": vector(16.4, 27.24) * mm, "endDerivative": vector(20.4, 0.4) * mm});
            skFitSpline(sketch, "E330", {"points": [v(63.32, 104.27) * mm, v(72.82, 84.27) * mm, v(63.32, 68.77) * mm], "startDerivative": vector(18.41, 0.3) * mm, "endDerivative": vector(-23.43, 0.2) * mm});
            skFitSpline(sketch, "E331", {"points": [v(63.32, 68.77) * mm, v(54.8, 66.18) * mm], "startDerivative": vector(-8.36, -0.1) * mm, "endDerivative": vector(-3.64, -4.62) * mm});
            skLineSegment(sketch, "E332", {"start": v(54.8, 66.18) * mm, "end": v(33.84, 39.58) * mm});
            skPoint(sketch, "E333.visualSharp", {"position": v(30.87, 35.8) * mm});
            skArc(sketch, "E333.filletArc", {"start": v(33.84, 39.58) * mm, "mid": v(31.97, 36.51) * mm, "end": v(30.89, 33.1) * mm});
            skPoint(sketch, "E334.visualSharp", {"position": v(23.82, 41.4) * mm});
            skArc(sketch, "E334.filletArc", {"start": v(21.15, 40.8) * mm, "mid": v(24.25, 42.66) * mm, "end": v(26.82, 45.2) * mm});
            skPoint(sketch, "E335.visualSharp", {"position": v(24.25, 27.4) * mm});
            skArc(sketch, "E335.filletArc", {"start": v(26.4, 27.82) * mm, "mid": v(24.51, 26.6) * mm, "end": v(23.35, 24.7) * mm});
            skPoint(sketch, "E336.visualSharp", {"position": v(17.16, 32.95) * mm});
            skArc(sketch, "E336.filletArc", {"start": v(16.77, 31.26) * mm, "mid": v(17, 32.65) * mm, "end": v(17.02, 34.05) * mm});
            skSolve(sketch);
        }
        {
            var Q0;
            Q0=qSketchRegion(id+"F2",true);
            extrude(context, id + "F3", {"entities" : qUnion([Q0]), "oppositeDirection" : true, "depth" : 4 * mm});
        }
        {
            var Q0;
            Q0=qCreatedBy(makeId("Top.planeOp"),FACE);
            var sketch = newSketch(context, id + "F4", { "sketchPlane" : qUnion([Q0])});
            skPoint(sketch, "E337.middle", {"position": v(-2.33, 0.15) * mm});
            skLineSegment(sketch, "E338.bottom", {"start": v(23.37, 32.78) * mm, "end": v(-28.03, 32.78) * mm, "construction": true});
            skLineSegment(sketch, "E338.top", {"start": v(23.37, -32.47) * mm, "end": v(-28.03, -32.47) * mm, "construction": true});
            skLineSegment(sketch, "E338.left", {"start": v(23.37, 32.78) * mm, "end": v(23.37, -32.47) * mm, "construction": true});
            skLineSegment(sketch, "E338.right", {"start": v(-28.03, 32.78) * mm, "end": v(-28.03, -32.47) * mm, "construction": true});
            skLineSegment(sketch, "E339.bottom", {"start": v(-67.33, 82.65) * mm, "end": v(62.67, 82.65) * mm, "construction": true});
            skLineSegment(sketch, "E339.top", {"start": v(-67.33, -82.35) * mm, "end": v(62.67, -82.35) * mm, "construction": true});
            skLineSegment(sketch, "E339.left", {"start": v(-67.33, 82.65) * mm, "end": v(-67.33, -82.35) * mm, "construction": true});
            skLineSegment(sketch, "E339.right", {"start": v(62.67, 82.65) * mm, "end": v(62.67, -82.35) * mm, "construction": true});
            skCircle(sketch, "E340", {"center": v(62.67, 82.65) * mm, "radius": 4.5 * mm, "construction": true});
            skCircle(sketch, "E341", {"center": v(-67.33, 82.65) * mm, "radius": 4.5 * mm, "construction": true});
            skCircle(sketch, "E342", {"center": v(62.67, -82.35) * mm, "radius": 4.5 * mm, "construction": true});
            skCircle(sketch, "E343", {"center": v(-67.33, -82.35) * mm, "radius": 4.5 * mm, "construction": true});
            skCircle(sketch, "E344", {"center": v(62.67, 82.65) * mm, "radius": 8 * mm, "construction": true});
            skCircle(sketch, "E345", {"center": v(62.67, -82.35) * mm, "radius": 8 * mm, "construction": true});
            skCircle(sketch, "E346", {"center": v(-67.33, -82.35) * mm, "radius": 8 * mm, "construction": true});
            skCircle(sketch, "E347", {"center": v(-67.33, 82.65) * mm, "radius": 8 * mm, "construction": true});
            skCircle(sketch, "E348", {"center": v(62.67, 82.65) * mm, "radius": 9.5 * mm, "construction": true});
            skCircle(sketch, "E349", {"center": v(62.67, -82.35) * mm, "radius": 9.5 * mm, "construction": true});
            skCircle(sketch, "E350", {"center": v(-67.33, -82.35) * mm, "radius": 9.5 * mm, "construction": true});
            skCircle(sketch, "E351", {"center": v(-67.33, 82.65) * mm, "radius": 9.5 * mm, "construction": true});
            skCircle(sketch, "E352", {"center": v(62.67, 82.65) * mm, "radius": 14 * mm, "construction": true});
            skCircle(sketch, "E353", {"center": v(-67.33, 82.65) * mm, "radius": 14 * mm, "construction": true});
            skCircle(sketch, "E354", {"center": v(62.67, -82.35) * mm, "radius": 14 * mm, "construction": true});
            skCircle(sketch, "E355", {"center": v(-67.33, -82.35) * mm, "radius": 14 * mm, "construction": true});
            skCircle(sketch, "E356", {"center": v(62.67, 82.65) * mm, "radius": 63.5 * mm, "construction": true});
            skCircle(sketch, "E357", {"center": v(62.67, -82.35) * mm, "radius": 63.5 * mm, "construction": true});
            skCircle(sketch, "E358", {"center": v(-67.33, -82.35) * mm, "radius": 63.5 * mm, "construction": true});
            skCircle(sketch, "E359", {"center": v(-67.33, 82.65) * mm, "radius": 63.5 * mm, "construction": true});
            skLineSegment(sketch, "E360.bottom", {"start": v(-28.52, 26.34) * mm, "end": v(23.86, 26.34) * mm, "construction": true});
            skLineSegment(sketch, "E360.top", {"start": v(-28.52, -26.04) * mm, "end": v(23.86, -26.04) * mm, "construction": true});
            skLineSegment(sketch, "E360.left", {"start": v(-28.52, 26.34) * mm, "end": v(-28.52, -26.04) * mm, "construction": true});
            skLineSegment(sketch, "E360.right", {"start": v(23.86, 26.34) * mm, "end": v(23.86, -26.04) * mm, "construction": true});
            skCircle(sketch, "E361", {"center": v(23.37, 32.78) * mm, "radius": 1.5 * mm, "construction": true});
            skCircle(sketch, "E362", {"center": v(-28.03, 32.78) * mm, "radius": 1.5 * mm, "construction": true});
            skCircle(sketch, "E363", {"center": v(23.37, -32.47) * mm, "radius": 1.5 * mm, "construction": true});
            skCircle(sketch, "E364", {"center": v(-28.03, -32.47) * mm, "radius": 1.5 * mm, "construction": true});
            skLineSegment(sketch, "E365", {"start": v(-67.33, 82.65) * mm, "end": v(62.67, -82.35) * mm, "construction": true});
            skLineSegment(sketch, "E366", {"start": v(62.67, 82.65) * mm, "end": v(-67.33, -82.35) * mm, "construction": true});
            skLineSegment(sketch, "E367.bottom", {"start": v(-17.58, -3.46) * mm, "end": v(12.92, -3.46) * mm, "construction": true});
            skLineSegment(sketch, "E367.top", {"start": v(-17.58, -33.96) * mm, "end": v(12.92, -33.96) * mm, "construction": true});
            skLineSegment(sketch, "E367.left", {"start": v(-17.58, -3.46) * mm, "end": v(-17.58, -33.96) * mm, "construction": true});
            skLineSegment(sketch, "E367.right", {"start": v(12.92, -3.46) * mm, "end": v(12.92, -33.96) * mm, "construction": true});
            skPoint(sketch, "E367.middle", {"position": v(-2.33, -18.71) * mm});
            skLineSegment(sketch, "E368.bottom", {"start": v(-17.58, 33.04) * mm, "end": v(12.92, 33.04) * mm, "construction": true});
            skLineSegment(sketch, "E368.top", {"start": v(-17.58, 2.54) * mm, "end": v(12.92, 2.54) * mm, "construction": true});
            skLineSegment(sketch, "E368.left", {"start": v(-17.58, 33.04) * mm, "end": v(-17.58, 2.54) * mm, "construction": true});
            skLineSegment(sketch, "E368.right", {"start": v(12.92, 33.04) * mm, "end": v(12.92, 2.54) * mm, "construction": true});
            skPoint(sketch, "E368.middle", {"position": v(-2.33, 17.79) * mm});
            skLineSegment(sketch, "E369", {"start": v(-2.33, 2.54) * mm, "end": v(-2.33, -3.46) * mm, "construction": true});
            skLineSegment(sketch, "E370", {"start": v(-28.03, 32.78) * mm, "end": v(-22.53, 37.1) * mm, "construction": true});
            skLineSegment(sketch, "E371", {"start": v(-28.03, 32.78) * mm, "end": v(-33.53, 28.44) * mm, "construction": true});
            skLineSegment(sketch, "E372", {"start": v(-28.03, 32.78) * mm, "end": v(-32.98, 39.06) * mm, "construction": true});
            skLineSegment(sketch, "E373", {"start": v(23.37, 32.78) * mm, "end": v(28.33, 39.06) * mm, "construction": true});
            skLineSegment(sketch, "E374", {"start": v(23.37, 32.78) * mm, "end": v(17.88, 37.1) * mm, "construction": true});
            skLineSegment(sketch, "E375", {"start": v(23.37, 32.78) * mm, "end": v(28.87, 28.44) * mm, "construction": true});
            skLineSegment(sketch, "E376", {"start": v(23.37, -32.47) * mm, "end": v(28.33, -38.75) * mm, "construction": true});
            skLineSegment(sketch, "E377", {"start": v(23.37, -32.47) * mm, "end": v(17.88, -36.8) * mm, "construction": true});
            skLineSegment(sketch, "E378", {"start": v(23.37, -32.47) * mm, "end": v(28.87, -28.13) * mm, "construction": true});
            skLineSegment(sketch, "E379", {"start": v(-28.03, -32.47) * mm, "end": v(-32.98, -38.75) * mm, "construction": true});
            skLineSegment(sketch, "E380", {"start": v(-28.03, -32.47) * mm, "end": v(-22.53, -36.8) * mm, "construction": true});
            skLineSegment(sketch, "E381", {"start": v(-28.03, -32.47) * mm, "end": v(-33.53, -28.13) * mm, "construction": true});
            skFitSpline(sketch, "E382", {"points": [v(-22.53, 37.1) * mm, v(-32.98, 39.06) * mm, v(-33.53, 28.44) * mm], "startDerivative": vector(-20.3, 7.46) * mm, "endDerivative": vector(0.93, -21.61) * mm});
            skFitSpline(sketch, "E383", {"points": [v(17.88, 37.1) * mm, v(28.33, 39.06) * mm, v(28.87, 28.44) * mm], "startDerivative": vector(20.3, 7.46) * mm, "endDerivative": vector(-0.93, -21.61) * mm});
            skPoint(sketch, "E384.visualSharp", {"position": v(-18.08, 35.74) * mm});
            skLineSegment(sketch, "E385", {"start": v(-18.08, 35.74) * mm, "end": v(-2.33, 35.74) * mm, "construction": true});
            skLineSegment(sketch, "E386", {"start": v(-2.33, 35.74) * mm, "end": v(13.42, 35.74) * mm, "construction": true});
            skPoint(sketch, "E387.visualSharp", {"position": v(13.42, 35.74) * mm});
            skLineSegment(sketch, "E388", {"start": v(-2.33, -33.96) * mm, "end": v(-2.33, -37.96) * mm, "construction": true});
            skLineSegment(sketch, "E389", {"start": v(-17.58, -33.96) * mm, "end": v(-21.58, -33.96) * mm, "construction": true});
            skLineSegment(sketch, "E390", {"start": v(12.92, -33.96) * mm, "end": v(16.92, -33.96) * mm, "construction": true});
            skLineSegment(sketch, "E391", {"start": v(-21.58, -38.3) * mm, "end": v(-2.33, -38.3) * mm, "construction": true});
            skLineSegment(sketch, "E392", {"start": v(-2.33, -38.3) * mm, "end": v(16.92, -38.3) * mm, "construction": true});
            skPoint(sketch, "E393.visualSharp", {"position": v(-21.58, -38.3) * mm});
            skPoint(sketch, "E394.visualSharp", {"position": v(16.92, -38.3) * mm});
            skCircle(sketch, "E395", {"center": v(-12.13, -44.75) * mm, "radius": 1.5 * mm});
            skCircle(sketch, "E396", {"center": v(7.47, -44.75) * mm, "radius": 1.5 * mm});
            skLineSegment(sketch, "E397", {"start": v(-12.13, -44.75) * mm, "end": v(-2.33, -44.75) * mm, "construction": true});
            skLineSegment(sketch, "E398", {"start": v(-2.33, -44.75) * mm, "end": v(7.47, -44.75) * mm, "construction": true});
            skFitSpline(sketch, "E399", {"points": [v(-33.53, 28.44) * mm, v(-28.03, 0.15) * mm, v(-33.53, -28.13) * mm], "startDerivative": vector(16.96, -67.18) * mm, "endDerivative": vector(-16.96, -67.18) * mm});
            skFitSpline(sketch, "E400", {"points": [v(28.87, 28.44) * mm, v(23.37, 0.15) * mm, v(28.87, -28.13) * mm], "startDerivative": vector(-16.96, -67.18) * mm, "endDerivative": vector(16.96, -67.18) * mm});
            skLineSegment(sketch, "E401", {"start": v(-2.33, -44.75) * mm, "end": v(-2.33, -50.75) * mm, "construction": true});
            skLineSegment(sketch, "E402", {"start": v(-12.13, -44.75) * mm, "end": v(-16.13, -44.75) * mm, "construction": true});
            skLineSegment(sketch, "E403", {"start": v(-12.13, -44.75) * mm, "end": v(-12.13, -48.75) * mm, "construction": true});
            skLineSegment(sketch, "E404", {"start": v(7.47, -44.75) * mm, "end": v(11.47, -44.75) * mm, "construction": true});
            skLineSegment(sketch, "E405", {"start": v(7.47, -44.75) * mm, "end": v(7.47, -48.75) * mm, "construction": true});
            skCircle(sketch, "E406", {"center": v(-28.03, 32.78) * mm, "radius": 1.5 * mm});
            skCircle(sketch, "E407", {"center": v(23.37, 32.78) * mm, "radius": 1.5 * mm});
            skCircle(sketch, "E408", {"center": v(-28.03, -32.47) * mm, "radius": 1.5 * mm});
            skCircle(sketch, "E409", {"center": v(23.37, -32.47) * mm, "radius": 1.5 * mm});
            skLineSegment(sketch, "E410", {"start": v(115.22, -24.48) * mm, "end": v(115.22, 9.49) * mm, "construction": true});
            skLineSegment(sketch, "E411", {"start": v(-21.37, -36.36) * mm, "end": v(-2.33, -36.36) * mm, "construction": true});
            skLineSegment(sketch, "E412", {"start": v(-2.33, -36.36) * mm, "end": v(16.72, -36.36) * mm, "construction": true});
            skFitSpline(sketch, "E413", {"points": [v(-21.58, -38.3) * mm, v(-16.13, -44.75) * mm, v(-12.13, -48.75) * mm, v(-2.33, -50.75) * mm], "startDerivative": vector(17.01, -18.5) * mm, "endDerivative": vector(29.8, -3.11) * mm});
            skFitSpline(sketch, "E414", {"points": [v(16.92, -38.3) * mm, v(11.47, -44.75) * mm, v(7.47, -48.75) * mm, v(-2.33, -50.75) * mm], "startDerivative": vector(-17.98, -19.6) * mm, "endDerivative": vector(-29.8, -3.11) * mm});
            skLineSegment(sketch, "E415", {"start": v(116.25, 10.49) * mm, "end": v(169.47, 8.84) * mm, "construction": true});
            skPoint(sketch, "E416.visualSharp", {"position": v(115.22, 10.52) * mm});
            skArc(sketch, "E416.filletArc", {"start": v(116.25, 10.49) * mm, "mid": v(115.53, 10.2) * mm, "end": v(115.22, 9.49) * mm, "construction": true});
            skPoint(sketch, "E417.visualSharp", {"position": v(16.72, -36.36) * mm});
            skPoint(sketch, "E418.visualSharp", {"position": v(-21.37, -36.36) * mm});
            skLineSegment(sketch, "E419.bottom", {"start": v(-16.1, 17.65) * mm, "end": v(11.45, 17.65) * mm, "construction": true});
            skLineSegment(sketch, "E419.top", {"start": v(-16.1, -17.35) * mm, "end": v(11.45, -17.35) * mm, "construction": true});
            skLineSegment(sketch, "E419.left", {"start": v(-16.1, 17.65) * mm, "end": v(-16.1, -17.35) * mm, "construction": true});
            skLineSegment(sketch, "E419.right", {"start": v(11.45, 17.65) * mm, "end": v(11.45, -17.35) * mm, "construction": true});
            skLineSegment(sketch, "E420", {"start": v(-2.33, 13.23) * mm, "end": v(-20.53, 13.23) * mm, "construction": true});
            skLineSegment(sketch, "E421", {"start": v(-2.33, 13.23) * mm, "end": v(15.88, 13.23) * mm, "construction": true});
            skLineSegment(sketch, "E422", {"start": v(-2.33, 0.15) * mm, "end": v(-2.33, 14.42) * mm, "construction": true});
            skLineSegment(sketch, "E423", {"start": v(-2.33, 0.15) * mm, "end": v(14.67, 0.15) * mm, "construction": true});
            skLineSegment(sketch, "E424.bottom", {"start": v(-18.22, 14.7) * mm, "end": v(13.57, 14.7) * mm, "construction": true});
            skLineSegment(sketch, "E424.top", {"start": v(-18.22, -14.4) * mm, "end": v(13.57, -14.4) * mm, "construction": true});
            skLineSegment(sketch, "E424.left", {"start": v(-18.22, 14.7) * mm, "end": v(-18.22, -14.4) * mm, "construction": true});
            skLineSegment(sketch, "E424.right", {"start": v(13.57, 14.7) * mm, "end": v(13.57, -14.4) * mm, "construction": true});
            skLineSegment(sketch, "E425", {"start": v(-2.33, 26.07) * mm, "end": v(12, 26.07) * mm, "construction": true});
            skLineSegment(sketch, "E426", {"start": v(-2.33, 26.07) * mm, "end": v(-16.66, 26.07) * mm, "construction": true});
            skPoint(sketch, "E427.middle", {"position": v(-16.66, 26.07) * mm});
            skPoint(sketch, "E428.middle", {"position": v(12, 26.07) * mm});
            skFitSpline(sketch, "E429", {"points": [v(-33.53, -28.13) * mm, v(-32.98, -38.75) * mm, v(-22.93, -36.94) * mm], "startDerivative": vector(-1.92, -24.87) * mm, "endDerivative": vector(23.17, 7.34) * mm});
            skLineSegment(sketch, "E430", {"start": v(-22.93, -36.94) * mm, "end": v(-2.33, -36.94) * mm, "construction": true});
            skLineSegment(sketch, "E431", {"start": v(-2.33, -36.94) * mm, "end": v(18.28, -36.94) * mm, "construction": true});
            skLineSegment(sketch, "E432", {"start": v(16.92, -38.3) * mm, "end": v(17.66, -37.14) * mm});
            skLineSegment(sketch, "E433", {"start": v(18.25, -36.93) * mm, "end": v(18.28, -36.94) * mm});
            skLineSegment(sketch, "E434", {"start": v(-21.58, -38.3) * mm, "end": v(-22.32, -37.14) * mm});
            skLineSegment(sketch, "E435", {"start": v(-22.9, -36.93) * mm, "end": v(-22.93, -36.94) * mm});
            skLineSegment(sketch, "E436", {"start": v(169.47, 8.84) * mm, "end": v(169.47, -13.62) * mm, "construction": true});
            skPoint(sketch, "E437.visualSharp", {"position": v(17.88, -36.8) * mm});
            skArc(sketch, "E437.filletArc", {"start": v(18.25, -36.93) * mm, "mid": v(17.92, -36.93) * mm, "end": v(17.66, -37.14) * mm});
            skPoint(sketch, "E438.visualSharp", {"position": v(-22.53, -36.8) * mm});
            skArc(sketch, "E438.filletArc", {"start": v(-22.32, -37.14) * mm, "mid": v(-22.58, -36.93) * mm, "end": v(-22.9, -36.93) * mm});
            skLineSegment(sketch, "E439", {"start": v(-2.33, 0.15) * mm, "end": v(-2.33, 3.45) * mm, "construction": true});
            skLineSegment(sketch, "E440.bottom", {"start": v(-7.83, 5.65) * mm, "end": v(3.17, 5.65) * mm, "construction": true});
            skLineSegment(sketch, "E440.top", {"start": v(-7.83, -5.35) * mm, "end": v(3.17, -5.35) * mm, "construction": true});
            skLineSegment(sketch, "E440.left", {"start": v(-7.83, 5.65) * mm, "end": v(-7.83, -5.35) * mm, "construction": true});
            skLineSegment(sketch, "E440.right", {"start": v(3.17, 5.65) * mm, "end": v(3.17, -5.35) * mm, "construction": true});
            skLineSegment(sketch, "E441.bottom", {"start": v(-10.3, 10.77) * mm, "end": v(5.65, 10.77) * mm});
            skPoint(sketch, "E441.middle", {"position": v(-2.33, 12.75) * mm});
            skPoint(sketch, "E442.middle", {"position": v(-2.33, -26.45) * mm});
            skPoint(sketch, "E443", {"position": v(-2.33, -17.35) * mm});
            skPoint(sketch, "E444", {"position": v(-2.33, -26.04) * mm});
            skLineSegment(sketch, "E445", {"start": v(-11.02, 12.48) * mm, "end": v(-3.74, 19.76) * mm});
            skLineSegment(sketch, "E446", {"start": v(-0.91, 19.76) * mm, "end": v(6.36, 12.48) * mm});
            skPoint(sketch, "E447.visualSharp", {"position": v(-2.33, 21.17) * mm});
            skArc(sketch, "E447.filletArc", {"start": v(-0.91, 19.76) * mm, "mid": v(-2.33, 20.34) * mm, "end": v(-3.74, 19.76) * mm});
            skPoint(sketch, "E448.visualSharp", {"position": v(-12.72, 10.77) * mm});
            skArc(sketch, "E448.filletArc", {"start": v(-11.02, 12.48) * mm, "mid": v(-11.23, 11.4) * mm, "end": v(-10.3, 10.77) * mm});
            skPoint(sketch, "E449.visualSharp", {"position": v(8.07, 10.77) * mm});
            skArc(sketch, "E449.filletArc", {"start": v(5.65, 10.77) * mm, "mid": v(6.58, 11.4) * mm, "end": v(6.36, 12.48) * mm});
            skPoint(sketch, "E450.visualSharp", {"position": v(-2.33, 0.75) * mm});
            skLineSegment(sketch, "E451", {"start": v(-1.33, 10.77) * mm, "end": v(-1.33, 6.27) * mm, "construction": true});
            skPoint(sketch, "E452.middle", {"position": v(-2.33, 9.75) * mm});
            skCircle(sketch, "E453", {"center": v(13.57, 14.7) * mm, "radius": 4.5 * mm, "construction": true});
            skCircle(sketch, "E454", {"center": v(-18.22, 14.7) * mm, "radius": 4.5 * mm, "construction": true});
            skCircle(sketch, "E455", {"center": v(13.57, -14.4) * mm, "radius": 4.5 * mm, "construction": true});
            skCircle(sketch, "E456", {"center": v(-18.22, -14.4) * mm, "radius": 4.5 * mm, "construction": true});
            skLineSegment(sketch, "E457", {"start": v(-2.33, 0.15) * mm, "end": v(-18.22, 14.7) * mm, "construction": true});
            skLineSegment(sketch, "E458", {"start": v(-2.33, 0.15) * mm, "end": v(13.57, 14.7) * mm, "construction": true});
            skLineSegment(sketch, "E459", {"start": v(13.57, 14.7) * mm, "end": v(23.37, 32.78) * mm, "construction": true});
            skLineSegment(sketch, "E460", {"start": v(-18.22, 14.7) * mm, "end": v(-28.03, 32.78) * mm, "construction": true});
            skLineSegment(sketch, "E461", {"start": v(-2.33, 0.15) * mm, "end": v(-18.22, -14.4) * mm, "construction": true});
            skLineSegment(sketch, "E462", {"start": v(-18.22, -14.4) * mm, "end": v(-28.03, -32.47) * mm, "construction": true});
            skLineSegment(sketch, "E463", {"start": v(-2.33, 0.15) * mm, "end": v(13.57, -14.4) * mm, "construction": true});
            skLineSegment(sketch, "E464", {"start": v(13.57, -14.4) * mm, "end": v(23.37, -32.47) * mm, "construction": true});
            skLineSegment(sketch, "E465", {"start": v(-12.93, 28.63) * mm, "end": v(-12.93, 20.27) * mm});
            skLineSegment(sketch, "E466", {"start": v(8.28, 28.63) * mm, "end": v(8.28, 20.27) * mm});
            skLineSegment(sketch, "E467", {"start": v(-11.23, 19.56) * mm, "end": v(-5.16, 25.63) * mm});
            skLineSegment(sketch, "E468", {"start": v(0.5, 25.63) * mm, "end": v(6.57, 19.56) * mm});
            skPoint(sketch, "E469.visualSharp", {"position": v(-4.57, 37.81) * mm});
            skPoint(sketch, "E470.visualSharp", {"position": v(-12.93, 29.46) * mm});
            skArc(sketch, "E470.filletArc", {"start": v(-12.35, 30.04) * mm, "mid": v(-12.78, 29.4) * mm, "end": v(-12.93, 28.63) * mm});
            skPoint(sketch, "E471.visualSharp", {"position": v(-4.57, 26.22) * mm});
            skArc(sketch, "E471.filletArc", {"start": v(-5.16, 25.63) * mm, "mid": v(-4.73, 26.28) * mm, "end": v(-4.57, 27.04) * mm});
            skPoint(sketch, "E472.visualSharp", {"position": v(-0.08, 26.22) * mm});
            skArc(sketch, "E472.filletArc", {"start": v(-0.08, 27.04) * mm, "mid": v(0.07, 26.28) * mm, "end": v(0.5, 25.63) * mm});
            skPoint(sketch, "E473.visualSharp", {"position": v(8.28, 29.46) * mm});
            skArc(sketch, "E473.filletArc", {"start": v(8.28, 28.63) * mm, "mid": v(8.13, 29.4) * mm, "end": v(7.7, 30.04) * mm});
            skPoint(sketch, "E474.visualSharp", {"position": v(-0.08, 37.81) * mm});
            skPoint(sketch, "E475.visualSharp", {"position": v(8.28, 17.86) * mm});
            skArc(sketch, "E475.filletArc", {"start": v(6.57, 19.56) * mm, "mid": v(7.66, 19.35) * mm, "end": v(8.28, 20.27) * mm});
            skPoint(sketch, "E476.visualSharp", {"position": v(-12.93, 17.86) * mm});
            skArc(sketch, "E476.filletArc", {"start": v(-12.93, 20.27) * mm, "mid": v(-12.32, 19.35) * mm, "end": v(-11.23, 19.56) * mm});
            skLineSegment(sketch, "E477", {"start": v(-2.33, -22.87) * mm, "end": v(-10.31, -22.87) * mm});
            skLineSegment(sketch, "E478", {"start": v(-2.33, -22.87) * mm, "end": v(5.66, -22.87) * mm});
            skLineSegment(sketch, "E479", {"start": v(-11.02, -24.57) * mm, "end": v(-3.74, -31.85) * mm});
            skLineSegment(sketch, "E480", {"start": v(6.37, -24.57) * mm, "end": v(-0.91, -31.85) * mm});
            skPoint(sketch, "E481.visualSharp", {"position": v(8.07, -22.87) * mm});
            skArc(sketch, "E481.filletArc", {"start": v(6.37, -24.57) * mm, "mid": v(6.58, -23.48) * mm, "end": v(5.66, -22.87) * mm});
            skPoint(sketch, "E482.visualSharp", {"position": v(-12.73, -22.87) * mm});
            skArc(sketch, "E482.filletArc", {"start": v(-10.31, -22.87) * mm, "mid": v(-11.24, -23.48) * mm, "end": v(-11.02, -24.57) * mm});
            skPoint(sketch, "E483.visualSharp", {"position": v(-2.33, -33.27) * mm});
            skArc(sketch, "E483.filletArc", {"start": v(-3.74, -31.85) * mm, "mid": v(-2.33, -32.44) * mm, "end": v(-0.91, -31.85) * mm});
            skFitSpline(sketch, "E484", {"points": [v(28.87, -28.13) * mm, v(28.33, -38.75) * mm, v(18.28, -36.94) * mm], "startDerivative": vector(1.93, -24.89) * mm, "endDerivative": vector(-23.2, 7.39) * mm});
            skLineSegment(sketch, "E485", {"start": v(-11.02, -30.5) * mm, "end": v(-6.24, -35.29) * mm});
            skLineSegment(sketch, "E486", {"start": v(6.37, -30.5) * mm, "end": v(1.59, -35.29) * mm});
            skLineSegment(sketch, "E487", {"start": v(-5.66, -36.7) * mm, "end": v(-5.66, -42.34) * mm});
            skLineSegment(sketch, "E488", {"start": v(-7.36, -43.05) * mm, "end": v(-12.14, -38.27) * mm});
            skLineSegment(sketch, "E489", {"start": v(-12.73, -36.85) * mm, "end": v(-12.73, -31.22) * mm});
            skLineSegment(sketch, "E490", {"start": v(1, -36.7) * mm, "end": v(1, -42.34) * mm});
            skLineSegment(sketch, "E491", {"start": v(2.7, -43.05) * mm, "end": v(7.49, -38.27) * mm});
            skLineSegment(sketch, "E492", {"start": v(8.07, -36.85) * mm, "end": v(8.07, -31.22) * mm});
            skPoint(sketch, "E493.visualSharp", {"position": v(8.07, -28.8) * mm});
            skArc(sketch, "E493.filletArc", {"start": v(8.07, -31.22) * mm, "mid": v(7.46, -30.3) * mm, "end": v(6.37, -30.5) * mm});
            skPoint(sketch, "E494.visualSharp", {"position": v(1, -44.75) * mm});
            skArc(sketch, "E494.filletArc", {"start": v(1, -42.34) * mm, "mid": v(1.62, -43.26) * mm, "end": v(2.7, -43.05) * mm});
            skPoint(sketch, "E495.visualSharp", {"position": v(-5.66, -44.75) * mm});
            skArc(sketch, "E495.filletArc", {"start": v(-7.36, -43.05) * mm, "mid": v(-6.27, -43.26) * mm, "end": v(-5.66, -42.34) * mm});
            skPoint(sketch, "E496.visualSharp", {"position": v(-12.73, -28.8) * mm});
            skArc(sketch, "E496.filletArc", {"start": v(-11.02, -30.5) * mm, "mid": v(-12.1, -30.3) * mm, "end": v(-12.73, -31.22) * mm});
            skPoint(sketch, "E497.visualSharp", {"position": v(-5.66, -35.87) * mm});
            skArc(sketch, "E497.filletArc", {"start": v(-5.66, -36.7) * mm, "mid": v(-5.8, -35.94) * mm, "end": v(-6.24, -35.29) * mm});
            skPoint(sketch, "E498.visualSharp", {"position": v(-12.73, -37.68) * mm});
            skArc(sketch, "E498.filletArc", {"start": v(-12.73, -36.85) * mm, "mid": v(-12.57, -37.62) * mm, "end": v(-12.14, -38.27) * mm});
            skPoint(sketch, "E499.visualSharp", {"position": v(1, -35.87) * mm});
            skArc(sketch, "E499.filletArc", {"start": v(1.59, -35.29) * mm, "mid": v(1.15, -35.94) * mm, "end": v(1, -36.7) * mm});
            skPoint(sketch, "E500.visualSharp", {"position": v(8.07, -37.68) * mm});
            skArc(sketch, "E500.filletArc", {"start": v(7.49, -38.27) * mm, "mid": v(7.92, -37.62) * mm, "end": v(8.07, -36.85) * mm});
            skLineSegment(sketch, "E501", {"start": v(-2.33, -18.71) * mm, "end": v(-10.31, -18.71) * mm});
            skLineSegment(sketch, "E502", {"start": v(-2.33, -18.71) * mm, "end": v(5.66, -18.71) * mm});
            skLineSegment(sketch, "E503", {"start": v(-11.02, -17) * mm, "end": v(-3.74, -9.72) * mm});
            skLineSegment(sketch, "E504", {"start": v(6.37, -17) * mm, "end": v(-0.91, -9.72) * mm});
            skPoint(sketch, "E505.visualSharp", {"position": v(-2.33, -8.31) * mm});
            skArc(sketch, "E505.filletArc", {"start": v(-0.91, -9.72) * mm, "mid": v(-2.33, -9.14) * mm, "end": v(-3.74, -9.72) * mm});
            skPoint(sketch, "E506.visualSharp", {"position": v(-12.73, -18.71) * mm});
            skArc(sketch, "E506.filletArc", {"start": v(-11.02, -17) * mm, "mid": v(-11.24, -18.1) * mm, "end": v(-10.31, -18.71) * mm});
            skPoint(sketch, "E507.visualSharp", {"position": v(8.07, -18.71) * mm});
            skArc(sketch, "E507.filletArc", {"start": v(5.66, -18.71) * mm, "mid": v(6.58, -18.1) * mm, "end": v(6.37, -17) * mm});
            skLineSegment(sketch, "E508", {"start": v(14.67, 0.15) * mm, "end": v(17.67, 0.15) * mm, "construction": true});
            skCircle(sketch, "E509", {"center": v(23.37, 32.78) * mm, "radius": 7 * mm, "construction": true});
            skLineSegment(sketch, "E510", {"start": v(17.64, 12.88) * mm, "end": v(21.69, 20.22) * mm});
            skLineSegment(sketch, "E511", {"start": v(22.15, 20.04) * mm, "end": v(18.73, 7.4) * mm});
            skLineSegment(sketch, "E512", {"start": v(16.8, 5.92) * mm, "end": v(12.23, 5.92) * mm});
            skLineSegment(sketch, "E513", {"start": v(11.62, 7.72) * mm, "end": v(16.31, 11.33) * mm});
            skPoint(sketch, "E514.visualSharp", {"position": v(22.7, 22.04) * mm});
            skArc(sketch, "E514.filletArc", {"start": v(22.15, 20.04) * mm, "mid": v(22, 20.33) * mm, "end": v(21.69, 20.22) * mm});
            skPoint(sketch, "E515.visualSharp", {"position": v(18.33, 5.92) * mm});
            skArc(sketch, "E515.filletArc", {"start": v(16.8, 5.92) * mm, "mid": v(18.02, 6.34) * mm, "end": v(18.73, 7.4) * mm});
            skPoint(sketch, "E516.visualSharp", {"position": v(9.29, 5.92) * mm});
            skArc(sketch, "E516.filletArc", {"start": v(11.62, 7.72) * mm, "mid": v(11.28, 6.6) * mm, "end": v(12.23, 5.92) * mm});
            skPoint(sketch, "E517.visualSharp", {"position": v(17.14, 11.97) * mm});
            skArc(sketch, "E517.filletArc", {"start": v(16.31, 11.33) * mm, "mid": v(17.06, 12.04) * mm, "end": v(17.64, 12.88) * mm});
            skLineSegment(sketch, "E518", {"start": v(9.29, 5.92) * mm, "end": v(-2.33, 5.92) * mm, "construction": true});
            skPoint(sketch, "E518.endSnap0", {"position": v(-2.33, 5.65) * mm});
            skLineSegment(sketch, "E519", {"start": v(-2.33, 5.92) * mm, "end": v(-13.94, 5.92) * mm, "construction": true});
            skLineSegment(sketch, "E520", {"start": v(-16.88, 5.92) * mm, "end": v(-21.46, 5.92) * mm});
            skLineSegment(sketch, "E521", {"start": v(17.14, 11.97) * mm, "end": v(-2.33, 11.97) * mm, "construction": true});
            skLineSegment(sketch, "E522", {"start": v(-2.33, 11.97) * mm, "end": v(-21.8, 11.97) * mm, "construction": true});
            skLineSegment(sketch, "E523", {"start": v(22.7, 22.04) * mm, "end": v(-2.33, 22.04) * mm, "construction": true});
            skLineSegment(sketch, "E524", {"start": v(-2.33, 22.04) * mm, "end": v(-27.34, 22.04) * mm, "construction": true});
            skLineSegment(sketch, "E525", {"start": v(-26.8, 20.04) * mm, "end": v(-23.39, 7.4) * mm});
            skLineSegment(sketch, "E526", {"start": v(-16.27, 7.72) * mm, "end": v(-20.97, 11.33) * mm});
            skLineSegment(sketch, "E527", {"start": v(-22.3, 12.88) * mm, "end": v(-26.34, 20.22) * mm});
            skPoint(sketch, "E528.visualSharp", {"position": v(-27.34, 22.04) * mm});
            skArc(sketch, "E528.filletArc", {"start": v(-26.34, 20.22) * mm, "mid": v(-26.65, 20.33) * mm, "end": v(-26.8, 20.04) * mm});
            skPoint(sketch, "E529.visualSharp", {"position": v(-13.94, 5.92) * mm});
            skArc(sketch, "E529.filletArc", {"start": v(-16.88, 5.92) * mm, "mid": v(-15.93, 6.6) * mm, "end": v(-16.27, 7.72) * mm});
            skPoint(sketch, "E530.visualSharp", {"position": v(-22.99, 5.92) * mm});
            skArc(sketch, "E530.filletArc", {"start": v(-23.39, 7.4) * mm, "mid": v(-22.67, 6.34) * mm, "end": v(-21.46, 5.92) * mm});
            skPoint(sketch, "E531.visualSharp", {"position": v(-21.8, 11.97) * mm});
            skArc(sketch, "E531.filletArc", {"start": v(-22.3, 12.88) * mm, "mid": v(-21.71, 12.04) * mm, "end": v(-20.97, 11.33) * mm});
            skFitSpline(sketch, "E532", {"points": [v(-22.53, 37.1) * mm, v(-2.33, 38.28) * mm, v(17.88, 37.1) * mm], "startDerivative": vector(40.4, 3.51) * mm, "endDerivative": vector(40.4, -3.51) * mm});
            skLineSegment(sketch, "E533", {"start": v(-0.08, 27.04) * mm, "end": v(-0.08, 30.57) * mm});
            skLineSegment(sketch, "E534", {"start": v(5.04, 32.7) * mm, "end": v(7.7, 30.04) * mm});
            skArc(sketch, "E535.filletArc", {"start": v(5.04, 32.7) * mm, "mid": v(1.77, 33.34) * mm, "end": v(-0.08, 30.57) * mm});
            skLineSegment(sketch, "E536", {"start": v(-12.35, 30.04) * mm, "end": v(-9.7, 32.7) * mm});
            skLineSegment(sketch, "E537", {"start": v(-4.57, 27.04) * mm, "end": v(-4.57, 30.57) * mm});
            skArc(sketch, "E538.filletArc", {"start": v(-4.57, 30.57) * mm, "mid": v(-6.43, 33.34) * mm, "end": v(-9.7, 32.7) * mm});
            skLineSegment(sketch, "E539", {"start": v(-2.33, 0.15) * mm, "end": v(-32.46, 0.15) * mm, "construction": true});
            skLineSegment(sketch, "E540", {"start": v(-27.34, 22.04) * mm, "end": v(-27.34, 0.15) * mm, "construction": true});
            skLineSegment(sketch, "E541", {"start": v(-27.34, 0.15) * mm, "end": v(-27.34, -21.73) * mm, "construction": true});
            skLineSegment(sketch, "E542", {"start": v(-21.8, 11.97) * mm, "end": v(-21.8, 0.15) * mm, "construction": true});
            skLineSegment(sketch, "E543", {"start": v(-21.8, 0.15) * mm, "end": v(-21.8, -11.66) * mm, "construction": true});
            skLineSegment(sketch, "E544", {"start": v(-22.99, 5.92) * mm, "end": v(-22.99, 0.15) * mm, "construction": true});
            skLineSegment(sketch, "E545", {"start": v(-22.99, 0.15) * mm, "end": v(-22.99, -5.62) * mm, "construction": true});
            skLineSegment(sketch, "E546", {"start": v(-13.94, 5.92) * mm, "end": v(-13.94, 0.15) * mm, "construction": true});
            skLineSegment(sketch, "E547", {"start": v(-13.94, 0.15) * mm, "end": v(-13.94, -5.62) * mm, "construction": true});
            skLineSegment(sketch, "E548", {"start": v(-26.8, -19.73) * mm, "end": v(-23.39, -7.1) * mm});
            skLineSegment(sketch, "E549", {"start": v(-21.46, -5.62) * mm, "end": v(-16.88, -5.62) * mm});
            skLineSegment(sketch, "E550", {"start": v(-16.27, -7.4) * mm, "end": v(-20.97, -11.02) * mm});
            skLineSegment(sketch, "E551", {"start": v(-22.3, -12.57) * mm, "end": v(-26.34, -19.91) * mm});
            skPoint(sketch, "E552.visualSharp", {"position": v(-22.99, -5.62) * mm});
            skArc(sketch, "E552.filletArc", {"start": v(-21.46, -5.62) * mm, "mid": v(-22.67, -6.03) * mm, "end": v(-23.39, -7.1) * mm});
            skPoint(sketch, "E553.visualSharp", {"position": v(-27.34, -21.73) * mm});
            skArc(sketch, "E553.filletArc", {"start": v(-26.8, -19.73) * mm, "mid": v(-26.65, -20.02) * mm, "end": v(-26.34, -19.91) * mm});
            skPoint(sketch, "E554.visualSharp", {"position": v(-13.94, -5.62) * mm});
            skArc(sketch, "E554.filletArc", {"start": v(-16.27, -7.4) * mm, "mid": v(-15.93, -6.3) * mm, "end": v(-16.88, -5.62) * mm});
            skPoint(sketch, "E555.visualSharp", {"position": v(-21.8, -11.66) * mm});
            skArc(sketch, "E555.filletArc", {"start": v(-20.97, -11.02) * mm, "mid": v(-21.71, -11.73) * mm, "end": v(-22.3, -12.57) * mm});
            skLineSegment(sketch, "E556", {"start": v(17.67, 0.15) * mm, "end": v(33.38, 0.15) * mm, "construction": true});
            skLineSegment(sketch, "E557", {"start": v(22.7, 22.04) * mm, "end": v(22.7, 0.15) * mm, "construction": true});
            skLineSegment(sketch, "E558", {"start": v(22.7, 0.15) * mm, "end": v(22.7, -21.73) * mm, "construction": true});
            skLineSegment(sketch, "E559", {"start": v(17.14, 11.97) * mm, "end": v(17.14, 0.15) * mm, "construction": true});
            skLineSegment(sketch, "E560", {"start": v(17.14, 0.15) * mm, "end": v(17.14, -11.66) * mm, "construction": true});
            skLineSegment(sketch, "E561", {"start": v(18.33, 5.92) * mm, "end": v(18.33, 0.15) * mm, "construction": true});
            skLineSegment(sketch, "E562", {"start": v(18.33, 0.15) * mm, "end": v(18.33, -5.62) * mm, "construction": true});
            skLineSegment(sketch, "E563", {"start": v(9.29, 5.92) * mm, "end": v(9.29, 0.15) * mm, "construction": true});
            skLineSegment(sketch, "E564", {"start": v(9.29, 0.15) * mm, "end": v(9.29, -5.62) * mm, "construction": true});
            skLineSegment(sketch, "E565", {"start": v(22.15, -19.73) * mm, "end": v(18.73, -7.1) * mm});
            skLineSegment(sketch, "E566", {"start": v(16.8, -5.62) * mm, "end": v(12.23, -5.62) * mm});
            skLineSegment(sketch, "E567", {"start": v(11.62, -7.4) * mm, "end": v(16.31, -11.02) * mm});
            skLineSegment(sketch, "E568", {"start": v(17.64, -12.57) * mm, "end": v(21.69, -19.91) * mm});
            skPoint(sketch, "E569.visualSharp", {"position": v(22.7, -21.73) * mm});
            skArc(sketch, "E569.filletArc", {"start": v(21.69, -19.91) * mm, "mid": v(22, -20.02) * mm, "end": v(22.15, -19.73) * mm});
            skPoint(sketch, "E570.visualSharp", {"position": v(9.29, -5.62) * mm});
            skArc(sketch, "E570.filletArc", {"start": v(12.23, -5.62) * mm, "mid": v(11.28, -6.3) * mm, "end": v(11.62, -7.4) * mm});
            skPoint(sketch, "E571.visualSharp", {"position": v(18.33, -5.62) * mm});
            skArc(sketch, "E571.filletArc", {"start": v(18.73, -7.1) * mm, "mid": v(18.02, -6.03) * mm, "end": v(16.8, -5.62) * mm});
            skPoint(sketch, "E572.visualSharp", {"position": v(17.14, -11.66) * mm});
            skArc(sketch, "E572.filletArc", {"start": v(17.64, -12.57) * mm, "mid": v(17.06, -11.73) * mm, "end": v(16.31, -11.02) * mm});
            skSolve(sketch);
        }
        {
            var Q0;
            Q0=qSketchRegion(id+"F4",true);
            extrude(context, id + "F5", {"entities" : qUnion([Q0]), "oppositeDirection" : true, "depth" : 10 * mm, "hasSecondDirection" : true, "secondDirectionOppositeDirection" : true, "secondDirectionDepth" : 8 * mm});
        }
    });
